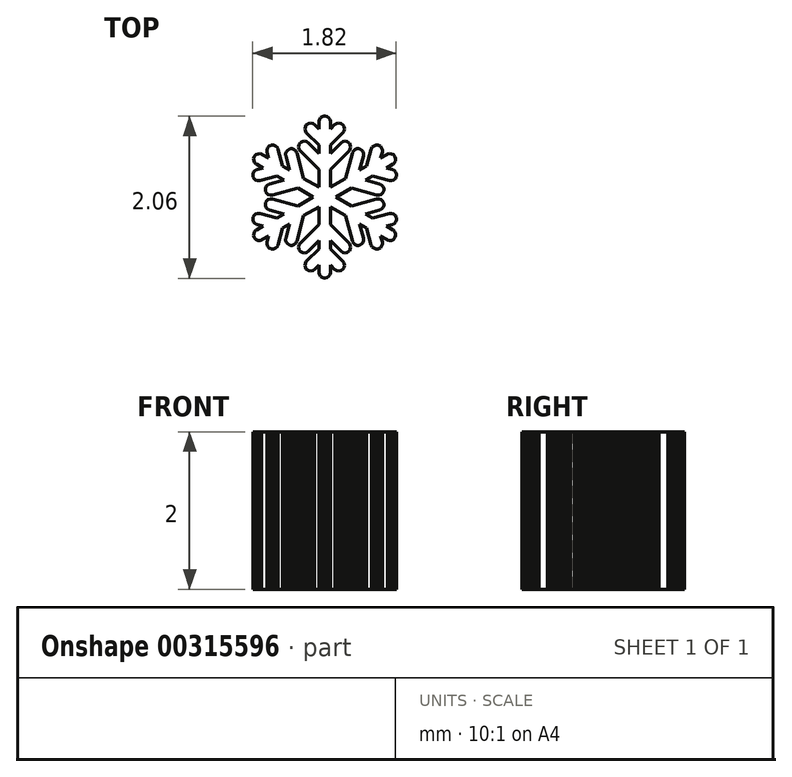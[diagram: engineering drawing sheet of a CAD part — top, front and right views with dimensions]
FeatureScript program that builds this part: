
annotation { "Feature Type Name" : "Feature", "Feature Type Description" : "" }
export const myFeature = defineFeature(function(context is Context, id is Id, definition is map)
    precondition{}
    {
        {
            var Q0;
            Q0=qCreatedBy(makeId("Top.planeOp"),FACE);
            var sketch = newSketch(context, id + "F0", { "sketchPlane" : qUnion([Q0])});
            skLineSegment(sketch, "E0", {"start": v(-2.78, 1.2) * mm, "end": v(-2.78, 3.11) * mm});
            skLineSegment(sketch, "E1", {"start": v(-2.78, 3.11) * mm, "end": v(-2.78, 3.12) * mm});
            skLineSegment(sketch, "E2", {"start": v(-2.78, 3.12) * mm, "end": v(-2.79, 3.14) * mm});
            skLineSegment(sketch, "E3", {"start": v(-2.79, 3.14) * mm, "end": v(-2.8, 3.16) * mm});
            skLineSegment(sketch, "E4", {"start": v(-2.8, 3.16) * mm, "end": v(-2.83, 3.18) * mm});
            skLineSegment(sketch, "E5", {"start": v(-2.83, 3.18) * mm, "end": v(-2.85, 3.18) * mm});
            skLineSegment(sketch, "E6", {"start": v(-2.85, 3.18) * mm, "end": v(-2.86, 3.18) * mm});
            skLineSegment(sketch, "E7", {"start": v(-2.86, 3.18) * mm, "end": v(-2.86, 3.18) * mm});
            skLineSegment(sketch, "E8", {"start": v(-2.86, 3.18) * mm, "end": v(-2.89, 3.18) * mm});
            skLineSegment(sketch, "E9", {"start": v(-2.89, 3.18) * mm, "end": v(-2.9, 3.16) * mm});
            skLineSegment(sketch, "E10", {"start": v(-2.9, 3.16) * mm, "end": v(-2.92, 3.14) * mm});
            skLineSegment(sketch, "E11", {"start": v(-2.92, 3.14) * mm, "end": v(-2.93, 3.12) * mm});
            skLineSegment(sketch, "E12", {"start": v(-2.93, 3.12) * mm, "end": v(-2.93, 3.11) * mm});
            skLineSegment(sketch, "E13", {"start": v(-2.93, 3.11) * mm, "end": v(-2.93, 1.2) * mm});
            skLineSegment(sketch, "E14", {"start": v(-2.93, 1.2) * mm, "end": v(-2.93, 1.19) * mm});
            skLineSegment(sketch, "E15", {"start": v(-2.93, 1.19) * mm, "end": v(-2.92, 1.17) * mm});
            skLineSegment(sketch, "E16", {"start": v(-2.92, 1.17) * mm, "end": v(-2.9, 1.14) * mm});
            skLineSegment(sketch, "E17", {"start": v(-2.9, 1.14) * mm, "end": v(-2.89, 1.13) * mm});
            skLineSegment(sketch, "E18", {"start": v(-2.89, 1.13) * mm, "end": v(-2.86, 1.12) * mm});
            skLineSegment(sketch, "E19", {"start": v(-2.86, 1.12) * mm, "end": v(-2.86, 1.12) * mm});
            skLineSegment(sketch, "E20", {"start": v(-2.86, 1.12) * mm, "end": v(-2.85, 1.12) * mm});
            skLineSegment(sketch, "E21", {"start": v(-2.85, 1.12) * mm, "end": v(-2.83, 1.13) * mm});
            skLineSegment(sketch, "E22", {"start": v(-2.83, 1.13) * mm, "end": v(-2.8, 1.14) * mm});
            skLineSegment(sketch, "E23", {"start": v(-2.8, 1.14) * mm, "end": v(-2.79, 1.17) * mm});
            skLineSegment(sketch, "E24", {"start": v(-2.79, 1.17) * mm, "end": v(-2.78, 1.19) * mm});
            skLineSegment(sketch, "E25", {"start": v(-2.78, 1.19) * mm, "end": v(-2.78, 1.2) * mm});
            skLineSegment(sketch, "E26", {"start": v(-2.55, 2.84) * mm, "end": v(-2.55, 2.85) * mm});
            skLineSegment(sketch, "E27", {"start": v(-2.55, 2.85) * mm, "end": v(-2.57, 2.86) * mm});
            skLineSegment(sketch, "E28", {"start": v(-2.57, 2.86) * mm, "end": v(-2.6, 2.86) * mm});
            skLineSegment(sketch, "E29", {"start": v(-2.6, 2.86) * mm, "end": v(-2.63, 2.86) * mm});
            skLineSegment(sketch, "E30", {"start": v(-2.63, 2.86) * mm, "end": v(-2.65, 2.85) * mm});
            skLineSegment(sketch, "E31", {"start": v(-2.65, 2.85) * mm, "end": v(-2.65, 2.84) * mm});
            skLineSegment(sketch, "E32", {"start": v(-2.65, 2.84) * mm, "end": v(-2.86, 2.64) * mm});
            skLineSegment(sketch, "E33", {"start": v(-2.86, 2.64) * mm, "end": v(-3.06, 2.84) * mm});
            skLineSegment(sketch, "E34", {"start": v(-3.06, 2.84) * mm, "end": v(-3.07, 2.85) * mm});
            skLineSegment(sketch, "E35", {"start": v(-3.07, 2.85) * mm, "end": v(-3.09, 2.86) * mm});
            skLineSegment(sketch, "E36", {"start": v(-3.09, 2.86) * mm, "end": v(-3.11, 2.86) * mm});
            skLineSegment(sketch, "E37", {"start": v(-3.11, 2.86) * mm, "end": v(-3.14, 2.86) * mm});
            skLineSegment(sketch, "E38", {"start": v(-3.14, 2.86) * mm, "end": v(-3.16, 2.85) * mm});
            skLineSegment(sketch, "E39", {"start": v(-3.16, 2.85) * mm, "end": v(-3.17, 2.84) * mm});
            skLineSegment(sketch, "E40", {"start": v(-3.17, 2.84) * mm, "end": v(-3.17, 2.84) * mm});
            skLineSegment(sketch, "E41", {"start": v(-3.17, 2.84) * mm, "end": v(-3.18, 2.82) * mm});
            skLineSegment(sketch, "E42", {"start": v(-3.18, 2.82) * mm, "end": v(-3.19, 2.79) * mm});
            skLineSegment(sketch, "E43", {"start": v(-3.19, 2.79) * mm, "end": v(-3.18, 2.76) * mm});
            skLineSegment(sketch, "E44", {"start": v(-3.18, 2.76) * mm, "end": v(-3.17, 2.74) * mm});
            skLineSegment(sketch, "E45", {"start": v(-3.17, 2.74) * mm, "end": v(-3.17, 2.74) * mm});
            skLineSegment(sketch, "E46", {"start": v(-3.17, 2.74) * mm, "end": v(-2.91, 2.48) * mm});
            skLineSegment(sketch, "E47", {"start": v(-2.91, 2.48) * mm, "end": v(-2.9, 2.48) * mm});
            skLineSegment(sketch, "E48", {"start": v(-2.9, 2.48) * mm, "end": v(-2.89, 2.47) * mm});
            skLineSegment(sketch, "E49", {"start": v(-2.89, 2.47) * mm, "end": v(-2.86, 2.46) * mm});
            skLineSegment(sketch, "E50", {"start": v(-2.86, 2.46) * mm, "end": v(-2.86, 2.46) * mm});
            skLineSegment(sketch, "E51", {"start": v(-2.86, 2.46) * mm, "end": v(-2.85, 2.46) * mm});
            skLineSegment(sketch, "E52", {"start": v(-2.85, 2.46) * mm, "end": v(-2.83, 2.47) * mm});
            skLineSegment(sketch, "E53", {"start": v(-2.83, 2.47) * mm, "end": v(-2.8, 2.48) * mm});
            skLineSegment(sketch, "E54", {"start": v(-2.8, 2.48) * mm, "end": v(-2.8, 2.48) * mm});
            skLineSegment(sketch, "E55", {"start": v(-2.8, 2.48) * mm, "end": v(-2.55, 2.74) * mm});
            skLineSegment(sketch, "E56", {"start": v(-2.55, 2.74) * mm, "end": v(-2.54, 2.74) * mm});
            skLineSegment(sketch, "E57", {"start": v(-2.54, 2.74) * mm, "end": v(-2.53, 2.76) * mm});
            skLineSegment(sketch, "E58", {"start": v(-2.53, 2.76) * mm, "end": v(-2.53, 2.79) * mm});
            skLineSegment(sketch, "E59", {"start": v(-2.53, 2.79) * mm, "end": v(-2.53, 2.82) * mm});
            skLineSegment(sketch, "E60", {"start": v(-2.53, 2.82) * mm, "end": v(-2.54, 2.84) * mm});
            skLineSegment(sketch, "E61", {"start": v(-2.54, 2.84) * mm, "end": v(-2.55, 2.84) * mm});
            skLineSegment(sketch, "E62", {"start": v(-2.63, 3.07) * mm, "end": v(-2.63, 3.08) * mm});
            skLineSegment(sketch, "E63", {"start": v(-2.63, 3.08) * mm, "end": v(-2.65, 3.09) * mm});
            skLineSegment(sketch, "E64", {"start": v(-2.65, 3.09) * mm, "end": v(-2.68, 3.1) * mm});
            skLineSegment(sketch, "E65", {"start": v(-2.68, 3.1) * mm, "end": v(-2.7, 3.09) * mm});
            skLineSegment(sketch, "E66", {"start": v(-2.7, 3.09) * mm, "end": v(-2.73, 3.08) * mm});
            skLineSegment(sketch, "E67", {"start": v(-2.73, 3.08) * mm, "end": v(-2.73, 3.07) * mm});
            skLineSegment(sketch, "E68", {"start": v(-2.73, 3.07) * mm, "end": v(-2.86, 2.94) * mm});
            skLineSegment(sketch, "E69", {"start": v(-2.86, 2.94) * mm, "end": v(-2.98, 3.07) * mm});
            skLineSegment(sketch, "E70", {"start": v(-2.98, 3.07) * mm, "end": v(-2.99, 3.08) * mm});
            skLineSegment(sketch, "E71", {"start": v(-2.99, 3.08) * mm, "end": v(-3, 3.09) * mm});
            skLineSegment(sketch, "E72", {"start": v(-3, 3.09) * mm, "end": v(-3.04, 3.1) * mm});
            skLineSegment(sketch, "E73", {"start": v(-3.04, 3.1) * mm, "end": v(-3.06, 3.09) * mm});
            skLineSegment(sketch, "E74", {"start": v(-3.06, 3.09) * mm, "end": v(-3.08, 3.08) * mm});
            skLineSegment(sketch, "E75", {"start": v(-3.08, 3.08) * mm, "end": v(-3.09, 3.07) * mm});
            skLineSegment(sketch, "E76", {"start": v(-3.09, 3.07) * mm, "end": v(-3.1, 3.07) * mm});
            skLineSegment(sketch, "E77", {"start": v(-3.1, 3.07) * mm, "end": v(-3.1, 3.05) * mm});
            skLineSegment(sketch, "E78", {"start": v(-3.1, 3.05) * mm, "end": v(-3.1, 3.02) * mm});
            skLineSegment(sketch, "E79", {"start": v(-3.1, 3.02) * mm, "end": v(-3.1, 3) * mm});
            skLineSegment(sketch, "E80", {"start": v(-3.1, 3) * mm, "end": v(-3.1, 2.97) * mm});
            skLineSegment(sketch, "E81", {"start": v(-3.1, 2.97) * mm, "end": v(-3.09, 2.97) * mm});
            skLineSegment(sketch, "E82", {"start": v(-3.09, 2.97) * mm, "end": v(-2.91, 2.8) * mm});
            skLineSegment(sketch, "E83", {"start": v(-2.91, 2.8) * mm, "end": v(-2.9, 2.79) * mm});
            skLineSegment(sketch, "E84", {"start": v(-2.9, 2.79) * mm, "end": v(-2.89, 2.78) * mm});
            skLineSegment(sketch, "E85", {"start": v(-2.89, 2.78) * mm, "end": v(-2.86, 2.77) * mm});
            skLineSegment(sketch, "E86", {"start": v(-2.86, 2.77) * mm, "end": v(-2.86, 2.77) * mm});
            skLineSegment(sketch, "E87", {"start": v(-2.86, 2.77) * mm, "end": v(-2.85, 2.77) * mm});
            skLineSegment(sketch, "E88", {"start": v(-2.85, 2.77) * mm, "end": v(-2.83, 2.78) * mm});
            skLineSegment(sketch, "E89", {"start": v(-2.83, 2.78) * mm, "end": v(-2.8, 2.79) * mm});
            skLineSegment(sketch, "E90", {"start": v(-2.8, 2.79) * mm, "end": v(-2.8, 2.8) * mm});
            skLineSegment(sketch, "E91", {"start": v(-2.8, 2.8) * mm, "end": v(-2.63, 2.97) * mm});
            skLineSegment(sketch, "E92", {"start": v(-2.63, 2.97) * mm, "end": v(-2.62, 2.97) * mm});
            skLineSegment(sketch, "E93", {"start": v(-2.62, 2.97) * mm, "end": v(-2.61, 3) * mm});
            skLineSegment(sketch, "E94", {"start": v(-2.61, 3) * mm, "end": v(-2.6, 3.02) * mm});
            skLineSegment(sketch, "E95", {"start": v(-2.6, 3.02) * mm, "end": v(-2.61, 3.05) * mm});
            skLineSegment(sketch, "E96", {"start": v(-2.61, 3.05) * mm, "end": v(-2.62, 3.07) * mm});
            skLineSegment(sketch, "E97", {"start": v(-2.62, 3.07) * mm, "end": v(-2.63, 3.07) * mm});
            skLineSegment(sketch, "E98", {"start": v(-2.55, 1.46) * mm, "end": v(-2.55, 1.46) * mm});
            skLineSegment(sketch, "E99", {"start": v(-2.55, 1.46) * mm, "end": v(-2.57, 1.45) * mm});
            skLineSegment(sketch, "E100", {"start": v(-2.57, 1.45) * mm, "end": v(-2.6, 1.44) * mm});
            skLineSegment(sketch, "E101", {"start": v(-2.6, 1.44) * mm, "end": v(-2.63, 1.45) * mm});
            skLineSegment(sketch, "E102", {"start": v(-2.63, 1.45) * mm, "end": v(-2.65, 1.46) * mm});
            skLineSegment(sketch, "E103", {"start": v(-2.65, 1.46) * mm, "end": v(-2.65, 1.46) * mm});
            skLineSegment(sketch, "E104", {"start": v(-2.65, 1.46) * mm, "end": v(-2.86, 1.67) * mm});
            skLineSegment(sketch, "E105", {"start": v(-2.86, 1.67) * mm, "end": v(-3.06, 1.46) * mm});
            skLineSegment(sketch, "E106", {"start": v(-3.06, 1.46) * mm, "end": v(-3.07, 1.46) * mm});
            skLineSegment(sketch, "E107", {"start": v(-3.07, 1.46) * mm, "end": v(-3.09, 1.45) * mm});
            skLineSegment(sketch, "E108", {"start": v(-3.09, 1.45) * mm, "end": v(-3.11, 1.44) * mm});
            skLineSegment(sketch, "E109", {"start": v(-3.11, 1.44) * mm, "end": v(-3.14, 1.45) * mm});
            skLineSegment(sketch, "E110", {"start": v(-3.14, 1.45) * mm, "end": v(-3.16, 1.46) * mm});
            skLineSegment(sketch, "E111", {"start": v(-3.16, 1.46) * mm, "end": v(-3.17, 1.46) * mm});
            skLineSegment(sketch, "E112", {"start": v(-3.17, 1.46) * mm, "end": v(-3.17, 1.47) * mm});
            skLineSegment(sketch, "E113", {"start": v(-3.17, 1.47) * mm, "end": v(-3.18, 1.49) * mm});
            skLineSegment(sketch, "E114", {"start": v(-3.18, 1.49) * mm, "end": v(-3.19, 1.52) * mm});
            skLineSegment(sketch, "E115", {"start": v(-3.19, 1.52) * mm, "end": v(-3.18, 1.54) * mm});
            skLineSegment(sketch, "E116", {"start": v(-3.18, 1.54) * mm, "end": v(-3.17, 1.56) * mm});
            skLineSegment(sketch, "E117", {"start": v(-3.17, 1.56) * mm, "end": v(-3.17, 1.57) * mm});
            skLineSegment(sketch, "E118", {"start": v(-3.17, 1.57) * mm, "end": v(-2.91, 1.82) * mm});
            skLineSegment(sketch, "E119", {"start": v(-2.91, 1.82) * mm, "end": v(-2.9, 1.83) * mm});
            skLineSegment(sketch, "E120", {"start": v(-2.9, 1.83) * mm, "end": v(-2.89, 1.84) * mm});
            skLineSegment(sketch, "E121", {"start": v(-2.89, 1.84) * mm, "end": v(-2.86, 1.84) * mm});
            skLineSegment(sketch, "E122", {"start": v(-2.86, 1.84) * mm, "end": v(-2.86, 1.84) * mm});
            skLineSegment(sketch, "E123", {"start": v(-2.86, 1.84) * mm, "end": v(-2.85, 1.84) * mm});
            skLineSegment(sketch, "E124", {"start": v(-2.85, 1.84) * mm, "end": v(-2.83, 1.84) * mm});
            skLineSegment(sketch, "E125", {"start": v(-2.83, 1.84) * mm, "end": v(-2.8, 1.83) * mm});
            skLineSegment(sketch, "E126", {"start": v(-2.8, 1.83) * mm, "end": v(-2.8, 1.82) * mm});
            skLineSegment(sketch, "E127", {"start": v(-2.8, 1.82) * mm, "end": v(-2.55, 1.57) * mm});
            skLineSegment(sketch, "E128", {"start": v(-2.55, 1.57) * mm, "end": v(-2.54, 1.56) * mm});
            skLineSegment(sketch, "E129", {"start": v(-2.54, 1.56) * mm, "end": v(-2.53, 1.54) * mm});
            skLineSegment(sketch, "E130", {"start": v(-2.53, 1.54) * mm, "end": v(-2.53, 1.52) * mm});
            skLineSegment(sketch, "E131", {"start": v(-2.53, 1.52) * mm, "end": v(-2.53, 1.49) * mm});
            skLineSegment(sketch, "E132", {"start": v(-2.53, 1.49) * mm, "end": v(-2.54, 1.47) * mm});
            skLineSegment(sketch, "E133", {"start": v(-2.54, 1.47) * mm, "end": v(-2.55, 1.46) * mm});
            skLineSegment(sketch, "E134", {"start": v(-2.63, 1.23) * mm, "end": v(-2.63, 1.23) * mm});
            skLineSegment(sketch, "E135", {"start": v(-2.63, 1.23) * mm, "end": v(-2.65, 1.22) * mm});
            skLineSegment(sketch, "E136", {"start": v(-2.65, 1.22) * mm, "end": v(-2.68, 1.21) * mm});
            skLineSegment(sketch, "E137", {"start": v(-2.68, 1.21) * mm, "end": v(-2.7, 1.22) * mm});
            skLineSegment(sketch, "E138", {"start": v(-2.7, 1.22) * mm, "end": v(-2.73, 1.23) * mm});
            skLineSegment(sketch, "E139", {"start": v(-2.73, 1.23) * mm, "end": v(-2.73, 1.23) * mm});
            skLineSegment(sketch, "E140", {"start": v(-2.73, 1.23) * mm, "end": v(-2.86, 1.36) * mm});
            skLineSegment(sketch, "E141", {"start": v(-2.86, 1.36) * mm, "end": v(-2.98, 1.23) * mm});
            skLineSegment(sketch, "E142", {"start": v(-2.98, 1.23) * mm, "end": v(-2.99, 1.23) * mm});
            skLineSegment(sketch, "E143", {"start": v(-2.99, 1.23) * mm, "end": v(-3, 1.22) * mm});
            skLineSegment(sketch, "E144", {"start": v(-3, 1.22) * mm, "end": v(-3.04, 1.21) * mm});
            skLineSegment(sketch, "E145", {"start": v(-3.04, 1.21) * mm, "end": v(-3.06, 1.22) * mm});
            skLineSegment(sketch, "E146", {"start": v(-3.06, 1.22) * mm, "end": v(-3.08, 1.23) * mm});
            skLineSegment(sketch, "E147", {"start": v(-3.08, 1.23) * mm, "end": v(-3.09, 1.23) * mm});
            skLineSegment(sketch, "E148", {"start": v(-3.09, 1.23) * mm, "end": v(-3.1, 1.24) * mm});
            skLineSegment(sketch, "E149", {"start": v(-3.1, 1.24) * mm, "end": v(-3.1, 1.26) * mm});
            skLineSegment(sketch, "E150", {"start": v(-3.1, 1.26) * mm, "end": v(-3.1, 1.29) * mm});
            skLineSegment(sketch, "E151", {"start": v(-3.1, 1.29) * mm, "end": v(-3.1, 1.31) * mm});
            skLineSegment(sketch, "E152", {"start": v(-3.1, 1.31) * mm, "end": v(-3.1, 1.33) * mm});
            skLineSegment(sketch, "E153", {"start": v(-3.1, 1.33) * mm, "end": v(-3.09, 1.34) * mm});
            skLineSegment(sketch, "E154", {"start": v(-3.09, 1.34) * mm, "end": v(-2.91, 1.51) * mm});
            skLineSegment(sketch, "E155", {"start": v(-2.91, 1.51) * mm, "end": v(-2.9, 1.52) * mm});
            skLineSegment(sketch, "E156", {"start": v(-2.9, 1.52) * mm, "end": v(-2.89, 1.53) * mm});
            skLineSegment(sketch, "E157", {"start": v(-2.89, 1.53) * mm, "end": v(-2.86, 1.53) * mm});
            skLineSegment(sketch, "E158", {"start": v(-2.86, 1.53) * mm, "end": v(-2.86, 1.53) * mm});
            skLineSegment(sketch, "E159", {"start": v(-2.86, 1.53) * mm, "end": v(-2.85, 1.53) * mm});
            skLineSegment(sketch, "E160", {"start": v(-2.85, 1.53) * mm, "end": v(-2.83, 1.53) * mm});
            skLineSegment(sketch, "E161", {"start": v(-2.83, 1.53) * mm, "end": v(-2.8, 1.52) * mm});
            skLineSegment(sketch, "E162", {"start": v(-2.8, 1.52) * mm, "end": v(-2.8, 1.51) * mm});
            skLineSegment(sketch, "E163", {"start": v(-2.8, 1.51) * mm, "end": v(-2.63, 1.34) * mm});
            skLineSegment(sketch, "E164", {"start": v(-2.63, 1.34) * mm, "end": v(-2.62, 1.33) * mm});
            skLineSegment(sketch, "E165", {"start": v(-2.62, 1.33) * mm, "end": v(-2.61, 1.31) * mm});
            skLineSegment(sketch, "E166", {"start": v(-2.61, 1.31) * mm, "end": v(-2.6, 1.29) * mm});
            skLineSegment(sketch, "E167", {"start": v(-2.6, 1.29) * mm, "end": v(-2.61, 1.26) * mm});
            skLineSegment(sketch, "E168", {"start": v(-2.61, 1.26) * mm, "end": v(-2.62, 1.24) * mm});
            skLineSegment(sketch, "E169", {"start": v(-2.62, 1.24) * mm, "end": v(-2.63, 1.23) * mm});
            skLineSegment(sketch, "E170", {"start": v(-2, 1.74) * mm, "end": v(-3.65, 2.7) * mm});
            skLineSegment(sketch, "E171", {"start": v(-3.65, 2.7) * mm, "end": v(-3.66, 2.7) * mm});
            skLineSegment(sketch, "E172", {"start": v(-3.66, 2.7) * mm, "end": v(-3.68, 2.7) * mm});
            skLineSegment(sketch, "E173", {"start": v(-3.68, 2.7) * mm, "end": v(-3.7, 2.7) * mm});
            skLineSegment(sketch, "E174", {"start": v(-3.7, 2.7) * mm, "end": v(-3.73, 2.7) * mm});
            skLineSegment(sketch, "E175", {"start": v(-3.73, 2.7) * mm, "end": v(-3.75, 2.67) * mm});
            skLineSegment(sketch, "E176", {"start": v(-3.75, 2.67) * mm, "end": v(-3.75, 2.67) * mm});
            skLineSegment(sketch, "E177", {"start": v(-3.75, 2.67) * mm, "end": v(-3.75, 2.66) * mm});
            skLineSegment(sketch, "E178", {"start": v(-3.75, 2.66) * mm, "end": v(-3.76, 2.64) * mm});
            skLineSegment(sketch, "E179", {"start": v(-3.76, 2.64) * mm, "end": v(-3.76, 2.61) * mm});
            skLineSegment(sketch, "E180", {"start": v(-3.76, 2.61) * mm, "end": v(-3.74, 2.59) * mm});
            skLineSegment(sketch, "E181", {"start": v(-3.74, 2.59) * mm, "end": v(-3.73, 2.57) * mm});
            skLineSegment(sketch, "E182", {"start": v(-3.73, 2.57) * mm, "end": v(-3.72, 2.57) * mm});
            skLineSegment(sketch, "E183", {"start": v(-3.72, 2.57) * mm, "end": v(-2.06, 1.61) * mm});
            skLineSegment(sketch, "E184", {"start": v(-2.06, 1.61) * mm, "end": v(-2.06, 1.6) * mm});
            skLineSegment(sketch, "E185", {"start": v(-2.06, 1.6) * mm, "end": v(-2.04, 1.6) * mm});
            skLineSegment(sketch, "E186", {"start": v(-2.04, 1.6) * mm, "end": v(-2, 1.6) * mm});
            skLineSegment(sketch, "E187", {"start": v(-2, 1.6) * mm, "end": v(-1.98, 1.62) * mm});
            skLineSegment(sketch, "E188", {"start": v(-1.98, 1.62) * mm, "end": v(-1.97, 1.63) * mm});
            skLineSegment(sketch, "E189", {"start": v(-1.97, 1.63) * mm, "end": v(-1.96, 1.64) * mm});
            skLineSegment(sketch, "E190", {"start": v(-1.96, 1.64) * mm, "end": v(-1.96, 1.64) * mm});
            skLineSegment(sketch, "E191", {"start": v(-1.96, 1.64) * mm, "end": v(-1.95, 1.66) * mm});
            skLineSegment(sketch, "E192", {"start": v(-1.95, 1.66) * mm, "end": v(-1.96, 1.7) * mm});
            skLineSegment(sketch, "E193", {"start": v(-1.96, 1.7) * mm, "end": v(-1.97, 1.72) * mm});
            skLineSegment(sketch, "E194", {"start": v(-1.97, 1.72) * mm, "end": v(-1.98, 1.73) * mm});
            skLineSegment(sketch, "E195", {"start": v(-1.98, 1.73) * mm, "end": v(-2, 1.74) * mm});
            skLineSegment(sketch, "E196", {"start": v(-3.3, 2.76) * mm, "end": v(-3.3, 2.76) * mm});
            skLineSegment(sketch, "E197", {"start": v(-3.3, 2.76) * mm, "end": v(-3.32, 2.75) * mm});
            skLineSegment(sketch, "E198", {"start": v(-3.32, 2.75) * mm, "end": v(-3.34, 2.73) * mm});
            skLineSegment(sketch, "E199", {"start": v(-3.34, 2.73) * mm, "end": v(-3.35, 2.7) * mm});
            skLineSegment(sketch, "E200", {"start": v(-3.35, 2.7) * mm, "end": v(-3.35, 2.68) * mm});
            skLineSegment(sketch, "E201", {"start": v(-3.35, 2.68) * mm, "end": v(-3.35, 2.68) * mm});
            skLineSegment(sketch, "E202", {"start": v(-3.35, 2.68) * mm, "end": v(-3.27, 2.4) * mm});
            skLineSegment(sketch, "E203", {"start": v(-3.27, 2.4) * mm, "end": v(-3.56, 2.32) * mm});
            skLineSegment(sketch, "E204", {"start": v(-3.56, 2.32) * mm, "end": v(-3.56, 2.32) * mm});
            skLineSegment(sketch, "E205", {"start": v(-3.56, 2.32) * mm, "end": v(-3.58, 2.3) * mm});
            skLineSegment(sketch, "E206", {"start": v(-3.58, 2.3) * mm, "end": v(-3.6, 2.29) * mm});
            skLineSegment(sketch, "E207", {"start": v(-3.6, 2.29) * mm, "end": v(-3.6, 2.26) * mm});
            skLineSegment(sketch, "E208", {"start": v(-3.6, 2.26) * mm, "end": v(-3.6, 2.24) * mm});
            skLineSegment(sketch, "E209", {"start": v(-3.6, 2.24) * mm, "end": v(-3.6, 2.23) * mm});
            skLineSegment(sketch, "E210", {"start": v(-3.6, 2.23) * mm, "end": v(-3.6, 2.22) * mm});
            skLineSegment(sketch, "E211", {"start": v(-3.6, 2.22) * mm, "end": v(-3.6, 2.2) * mm});
            skLineSegment(sketch, "E212", {"start": v(-3.6, 2.2) * mm, "end": v(-3.57, 2.19) * mm});
            skLineSegment(sketch, "E213", {"start": v(-3.57, 2.19) * mm, "end": v(-3.55, 2.18) * mm});
            skLineSegment(sketch, "E214", {"start": v(-3.55, 2.18) * mm, "end": v(-3.53, 2.18) * mm});
            skLineSegment(sketch, "E215", {"start": v(-3.53, 2.18) * mm, "end": v(-3.52, 2.18) * mm});
            skLineSegment(sketch, "E216", {"start": v(-3.52, 2.18) * mm, "end": v(-3.17, 2.27) * mm});
            skLineSegment(sketch, "E217", {"start": v(-3.17, 2.27) * mm, "end": v(-3.17, 2.27) * mm});
            skLineSegment(sketch, "E218", {"start": v(-3.17, 2.27) * mm, "end": v(-3.14, 2.29) * mm});
            skLineSegment(sketch, "E219", {"start": v(-3.14, 2.29) * mm, "end": v(-3.13, 2.3) * mm});
            skLineSegment(sketch, "E220", {"start": v(-3.13, 2.3) * mm, "end": v(-3.13, 2.3) * mm});
            skLineSegment(sketch, "E221", {"start": v(-3.13, 2.3) * mm, "end": v(-3.12, 2.31) * mm});
            skLineSegment(sketch, "E222", {"start": v(-3.12, 2.31) * mm, "end": v(-3.11, 2.34) * mm});
            skLineSegment(sketch, "E223", {"start": v(-3.11, 2.34) * mm, "end": v(-3.12, 2.36) * mm});
            skLineSegment(sketch, "E224", {"start": v(-3.12, 2.36) * mm, "end": v(-3.12, 2.37) * mm});
            skLineSegment(sketch, "E225", {"start": v(-3.12, 2.37) * mm, "end": v(-3.2, 2.71) * mm});
            skLineSegment(sketch, "E226", {"start": v(-3.2, 2.71) * mm, "end": v(-3.21, 2.72) * mm});
            skLineSegment(sketch, "E227", {"start": v(-3.21, 2.72) * mm, "end": v(-3.22, 2.74) * mm});
            skLineSegment(sketch, "E228", {"start": v(-3.22, 2.74) * mm, "end": v(-3.24, 2.76) * mm});
            skLineSegment(sketch, "E229", {"start": v(-3.24, 2.76) * mm, "end": v(-3.27, 2.77) * mm});
            skLineSegment(sketch, "E230", {"start": v(-3.27, 2.77) * mm, "end": v(-3.3, 2.77) * mm});
            skLineSegment(sketch, "E231", {"start": v(-3.3, 2.77) * mm, "end": v(-3.3, 2.76) * mm});
            skLineSegment(sketch, "E232", {"start": v(-3.54, 2.81) * mm, "end": v(-3.54, 2.8) * mm});
            skLineSegment(sketch, "E233", {"start": v(-3.54, 2.8) * mm, "end": v(-3.56, 2.8) * mm});
            skLineSegment(sketch, "E234", {"start": v(-3.56, 2.8) * mm, "end": v(-3.58, 2.78) * mm});
            skLineSegment(sketch, "E235", {"start": v(-3.58, 2.78) * mm, "end": v(-3.6, 2.75) * mm});
            skLineSegment(sketch, "E236", {"start": v(-3.6, 2.75) * mm, "end": v(-3.6, 2.73) * mm});
            skLineSegment(sketch, "E237", {"start": v(-3.6, 2.73) * mm, "end": v(-3.59, 2.72) * mm});
            skLineSegment(sketch, "E238", {"start": v(-3.59, 2.72) * mm, "end": v(-3.54, 2.55) * mm});
            skLineSegment(sketch, "E239", {"start": v(-3.54, 2.55) * mm, "end": v(-3.72, 2.5) * mm});
            skLineSegment(sketch, "E240", {"start": v(-3.72, 2.5) * mm, "end": v(-3.72, 2.5) * mm});
            skLineSegment(sketch, "E241", {"start": v(-3.72, 2.5) * mm, "end": v(-3.74, 2.49) * mm});
            skLineSegment(sketch, "E242", {"start": v(-3.74, 2.49) * mm, "end": v(-3.76, 2.47) * mm});
            skLineSegment(sketch, "E243", {"start": v(-3.76, 2.47) * mm, "end": v(-3.77, 2.44) * mm});
            skLineSegment(sketch, "E244", {"start": v(-3.77, 2.44) * mm, "end": v(-3.77, 2.42) * mm});
            skLineSegment(sketch, "E245", {"start": v(-3.77, 2.42) * mm, "end": v(-3.77, 2.41) * mm});
            skLineSegment(sketch, "E246", {"start": v(-3.77, 2.41) * mm, "end": v(-3.77, 2.4) * mm});
            skLineSegment(sketch, "E247", {"start": v(-3.77, 2.4) * mm, "end": v(-3.75, 2.39) * mm});
            skLineSegment(sketch, "E248", {"start": v(-3.75, 2.39) * mm, "end": v(-3.73, 2.37) * mm});
            skLineSegment(sketch, "E249", {"start": v(-3.73, 2.37) * mm, "end": v(-3.7, 2.36) * mm});
            skLineSegment(sketch, "E250", {"start": v(-3.7, 2.36) * mm, "end": v(-3.68, 2.36) * mm});
            skLineSegment(sketch, "E251", {"start": v(-3.68, 2.36) * mm, "end": v(-3.68, 2.36) * mm});
            skLineSegment(sketch, "E252", {"start": v(-3.68, 2.36) * mm, "end": v(-3.44, 2.43) * mm});
            skLineSegment(sketch, "E253", {"start": v(-3.44, 2.43) * mm, "end": v(-3.43, 2.43) * mm});
            skLineSegment(sketch, "E254", {"start": v(-3.43, 2.43) * mm, "end": v(-3.41, 2.44) * mm});
            skLineSegment(sketch, "E255", {"start": v(-3.41, 2.44) * mm, "end": v(-3.4, 2.46) * mm});
            skLineSegment(sketch, "E256", {"start": v(-3.4, 2.46) * mm, "end": v(-3.4, 2.46) * mm});
            skLineSegment(sketch, "E257", {"start": v(-3.4, 2.46) * mm, "end": v(-3.4, 2.47) * mm});
            skLineSegment(sketch, "E258", {"start": v(-3.4, 2.47) * mm, "end": v(-3.38, 2.49) * mm});
            skLineSegment(sketch, "E259", {"start": v(-3.38, 2.49) * mm, "end": v(-3.38, 2.52) * mm});
            skLineSegment(sketch, "E260", {"start": v(-3.38, 2.52) * mm, "end": v(-3.38, 2.52) * mm});
            skLineSegment(sketch, "E261", {"start": v(-3.38, 2.52) * mm, "end": v(-3.45, 2.76) * mm});
            skLineSegment(sketch, "E262", {"start": v(-3.45, 2.76) * mm, "end": v(-3.45, 2.77) * mm});
            skLineSegment(sketch, "E263", {"start": v(-3.45, 2.77) * mm, "end": v(-3.46, 2.79) * mm});
            skLineSegment(sketch, "E264", {"start": v(-3.46, 2.79) * mm, "end": v(-3.48, 2.8) * mm});
            skLineSegment(sketch, "E265", {"start": v(-3.48, 2.8) * mm, "end": v(-3.5, 2.81) * mm});
            skLineSegment(sketch, "E266", {"start": v(-3.5, 2.81) * mm, "end": v(-3.53, 2.81) * mm});
            skLineSegment(sketch, "E267", {"start": v(-3.53, 2.81) * mm, "end": v(-3.54, 2.81) * mm});
            skLineSegment(sketch, "E268", {"start": v(-2.1, 2.08) * mm, "end": v(-2.1, 2.07) * mm});
            skLineSegment(sketch, "E269", {"start": v(-2.1, 2.07) * mm, "end": v(-2.1, 2.05) * mm});
            skLineSegment(sketch, "E270", {"start": v(-2.1, 2.05) * mm, "end": v(-2.11, 2.02) * mm});
            skLineSegment(sketch, "E271", {"start": v(-2.11, 2.02) * mm, "end": v(-2.13, 2) * mm});
            skLineSegment(sketch, "E272", {"start": v(-2.13, 2) * mm, "end": v(-2.15, 1.99) * mm});
            skLineSegment(sketch, "E273", {"start": v(-2.15, 1.99) * mm, "end": v(-2.16, 1.99) * mm});
            skLineSegment(sketch, "E274", {"start": v(-2.16, 1.99) * mm, "end": v(-2.44, 1.91) * mm});
            skLineSegment(sketch, "E275", {"start": v(-2.44, 1.91) * mm, "end": v(-2.36, 1.63) * mm});
            skLineSegment(sketch, "E276", {"start": v(-2.36, 1.63) * mm, "end": v(-2.36, 1.62) * mm});
            skLineSegment(sketch, "E277", {"start": v(-2.36, 1.62) * mm, "end": v(-2.36, 1.6) * mm});
            skLineSegment(sketch, "E278", {"start": v(-2.36, 1.6) * mm, "end": v(-2.37, 1.58) * mm});
            skLineSegment(sketch, "E279", {"start": v(-2.37, 1.58) * mm, "end": v(-2.39, 1.55) * mm});
            skLineSegment(sketch, "E280", {"start": v(-2.39, 1.55) * mm, "end": v(-2.4, 1.54) * mm});
            skLineSegment(sketch, "E281", {"start": v(-2.4, 1.54) * mm, "end": v(-2.42, 1.54) * mm});
            skLineSegment(sketch, "E282", {"start": v(-2.42, 1.54) * mm, "end": v(-2.42, 1.54) * mm});
            skLineSegment(sketch, "E283", {"start": v(-2.42, 1.54) * mm, "end": v(-2.44, 1.54) * mm});
            skLineSegment(sketch, "E284", {"start": v(-2.44, 1.54) * mm, "end": v(-2.47, 1.55) * mm});
            skLineSegment(sketch, "E285", {"start": v(-2.47, 1.55) * mm, "end": v(-2.5, 1.57) * mm});
            skLineSegment(sketch, "E286", {"start": v(-2.5, 1.57) * mm, "end": v(-2.5, 1.59) * mm});
            skLineSegment(sketch, "E287", {"start": v(-2.5, 1.59) * mm, "end": v(-2.5, 1.6) * mm});
            skLineSegment(sketch, "E288", {"start": v(-2.5, 1.6) * mm, "end": v(-2.6, 1.94) * mm});
            skLineSegment(sketch, "E289", {"start": v(-2.6, 1.94) * mm, "end": v(-2.6, 1.95) * mm});
            skLineSegment(sketch, "E290", {"start": v(-2.6, 1.95) * mm, "end": v(-2.6, 1.97) * mm});
            skLineSegment(sketch, "E291", {"start": v(-2.6, 1.97) * mm, "end": v(-2.6, 2) * mm});
            skLineSegment(sketch, "E292", {"start": v(-2.6, 2) * mm, "end": v(-2.59, 2) * mm});
            skLineSegment(sketch, "E293", {"start": v(-2.59, 2) * mm, "end": v(-2.59, 2) * mm});
            skLineSegment(sketch, "E294", {"start": v(-2.59, 2) * mm, "end": v(-2.57, 2.02) * mm});
            skLineSegment(sketch, "E295", {"start": v(-2.57, 2.02) * mm, "end": v(-2.55, 2.03) * mm});
            skLineSegment(sketch, "E296", {"start": v(-2.55, 2.03) * mm, "end": v(-2.54, 2.03) * mm});
            skLineSegment(sketch, "E297", {"start": v(-2.54, 2.03) * mm, "end": v(-2.2, 2.13) * mm});
            skLineSegment(sketch, "E298", {"start": v(-2.2, 2.13) * mm, "end": v(-2.19, 2.13) * mm});
            skLineSegment(sketch, "E299", {"start": v(-2.19, 2.13) * mm, "end": v(-2.17, 2.13) * mm});
            skLineSegment(sketch, "E300", {"start": v(-2.17, 2.13) * mm, "end": v(-2.14, 2.12) * mm});
            skLineSegment(sketch, "E301", {"start": v(-2.14, 2.12) * mm, "end": v(-2.12, 2.1) * mm});
            skLineSegment(sketch, "E302", {"start": v(-2.12, 2.1) * mm, "end": v(-2.1, 2.08) * mm});
            skLineSegment(sketch, "E303", {"start": v(-2.1, 2.08) * mm, "end": v(-2.1, 2.08) * mm});
            skLineSegment(sketch, "E304", {"start": v(-1.95, 1.9) * mm, "end": v(-1.95, 1.89) * mm});
            skLineSegment(sketch, "E305", {"start": v(-1.95, 1.89) * mm, "end": v(-1.95, 1.86) * mm});
            skLineSegment(sketch, "E306", {"start": v(-1.95, 1.86) * mm, "end": v(-1.95, 1.84) * mm});
            skLineSegment(sketch, "E307", {"start": v(-1.95, 1.84) * mm, "end": v(-1.97, 1.82) * mm});
            skLineSegment(sketch, "E308", {"start": v(-1.97, 1.82) * mm, "end": v(-2, 1.8) * mm});
            skLineSegment(sketch, "E309", {"start": v(-2, 1.8) * mm, "end": v(-2, 1.8) * mm});
            skLineSegment(sketch, "E310", {"start": v(-2, 1.8) * mm, "end": v(-2.17, 1.76) * mm});
            skLineSegment(sketch, "E311", {"start": v(-2.17, 1.76) * mm, "end": v(-2.13, 1.58) * mm});
            skLineSegment(sketch, "E312", {"start": v(-2.13, 1.58) * mm, "end": v(-2.12, 1.58) * mm});
            skLineSegment(sketch, "E313", {"start": v(-2.12, 1.58) * mm, "end": v(-2.12, 1.56) * mm});
            skLineSegment(sketch, "E314", {"start": v(-2.12, 1.56) * mm, "end": v(-2.13, 1.53) * mm});
            skLineSegment(sketch, "E315", {"start": v(-2.13, 1.53) * mm, "end": v(-2.15, 1.5) * mm});
            skLineSegment(sketch, "E316", {"start": v(-2.15, 1.5) * mm, "end": v(-2.17, 1.5) * mm});
            skLineSegment(sketch, "E317", {"start": v(-2.17, 1.5) * mm, "end": v(-2.18, 1.5) * mm});
            skLineSegment(sketch, "E318", {"start": v(-2.18, 1.5) * mm, "end": v(-2.18, 1.5) * mm});
            skLineSegment(sketch, "E319", {"start": v(-2.18, 1.5) * mm, "end": v(-2.2, 1.5) * mm});
            skLineSegment(sketch, "E320", {"start": v(-2.2, 1.5) * mm, "end": v(-2.23, 1.5) * mm});
            skLineSegment(sketch, "E321", {"start": v(-2.23, 1.5) * mm, "end": v(-2.25, 1.52) * mm});
            skLineSegment(sketch, "E322", {"start": v(-2.25, 1.52) * mm, "end": v(-2.26, 1.54) * mm});
            skLineSegment(sketch, "E323", {"start": v(-2.26, 1.54) * mm, "end": v(-2.27, 1.55) * mm});
            skLineSegment(sketch, "E324", {"start": v(-2.27, 1.55) * mm, "end": v(-2.33, 1.79) * mm});
            skLineSegment(sketch, "E325", {"start": v(-2.33, 1.79) * mm, "end": v(-2.33, 1.8) * mm});
            skLineSegment(sketch, "E326", {"start": v(-2.33, 1.8) * mm, "end": v(-2.33, 1.82) * mm});
            skLineSegment(sketch, "E327", {"start": v(-2.33, 1.82) * mm, "end": v(-2.32, 1.84) * mm});
            skLineSegment(sketch, "E328", {"start": v(-2.32, 1.84) * mm, "end": v(-2.32, 1.84) * mm});
            skLineSegment(sketch, "E329", {"start": v(-2.32, 1.84) * mm, "end": v(-2.32, 1.85) * mm});
            skLineSegment(sketch, "E330", {"start": v(-2.32, 1.85) * mm, "end": v(-2.3, 1.87) * mm});
            skLineSegment(sketch, "E331", {"start": v(-2.3, 1.87) * mm, "end": v(-2.28, 1.88) * mm});
            skLineSegment(sketch, "E332", {"start": v(-2.28, 1.88) * mm, "end": v(-2.28, 1.88) * mm});
            skLineSegment(sketch, "E333", {"start": v(-2.28, 1.88) * mm, "end": v(-2.04, 1.94) * mm});
            skLineSegment(sketch, "E334", {"start": v(-2.04, 1.94) * mm, "end": v(-2.03, 1.95) * mm});
            skLineSegment(sketch, "E335", {"start": v(-2.03, 1.95) * mm, "end": v(-2, 1.95) * mm});
            skLineSegment(sketch, "E336", {"start": v(-2, 1.95) * mm, "end": v(-1.98, 1.94) * mm});
            skLineSegment(sketch, "E337", {"start": v(-1.98, 1.94) * mm, "end": v(-1.96, 1.92) * mm});
            skLineSegment(sketch, "E338", {"start": v(-1.96, 1.92) * mm, "end": v(-1.95, 1.9) * mm});
            skLineSegment(sketch, "E339", {"start": v(-1.95, 1.9) * mm, "end": v(-1.95, 1.9) * mm});
            skLineSegment(sketch, "E340", {"start": v(-2.06, 2.7) * mm, "end": v(-3.72, 1.74) * mm});
            skLineSegment(sketch, "E341", {"start": v(-3.72, 1.74) * mm, "end": v(-3.73, 1.73) * mm});
            skLineSegment(sketch, "E342", {"start": v(-3.73, 1.73) * mm, "end": v(-3.74, 1.72) * mm});
            skLineSegment(sketch, "E343", {"start": v(-3.74, 1.72) * mm, "end": v(-3.76, 1.7) * mm});
            skLineSegment(sketch, "E344", {"start": v(-3.76, 1.7) * mm, "end": v(-3.76, 1.66) * mm});
            skLineSegment(sketch, "E345", {"start": v(-3.76, 1.66) * mm, "end": v(-3.75, 1.64) * mm});
            skLineSegment(sketch, "E346", {"start": v(-3.75, 1.64) * mm, "end": v(-3.75, 1.64) * mm});
            skLineSegment(sketch, "E347", {"start": v(-3.75, 1.64) * mm, "end": v(-3.75, 1.63) * mm});
            skLineSegment(sketch, "E348", {"start": v(-3.75, 1.63) * mm, "end": v(-3.73, 1.62) * mm});
            skLineSegment(sketch, "E349", {"start": v(-3.73, 1.62) * mm, "end": v(-3.7, 1.6) * mm});
            skLineSegment(sketch, "E350", {"start": v(-3.7, 1.6) * mm, "end": v(-3.68, 1.6) * mm});
            skLineSegment(sketch, "E351", {"start": v(-3.68, 1.6) * mm, "end": v(-3.66, 1.6) * mm});
            skLineSegment(sketch, "E352", {"start": v(-3.66, 1.6) * mm, "end": v(-3.65, 1.61) * mm});
            skLineSegment(sketch, "E353", {"start": v(-3.65, 1.61) * mm, "end": v(-2, 2.57) * mm});
            skLineSegment(sketch, "E354", {"start": v(-2, 2.57) * mm, "end": v(-1.98, 2.57) * mm});
            skLineSegment(sketch, "E355", {"start": v(-1.98, 2.57) * mm, "end": v(-1.97, 2.59) * mm});
            skLineSegment(sketch, "E356", {"start": v(-1.97, 2.59) * mm, "end": v(-1.96, 2.61) * mm});
            skLineSegment(sketch, "E357", {"start": v(-1.96, 2.61) * mm, "end": v(-1.95, 2.64) * mm});
            skLineSegment(sketch, "E358", {"start": v(-1.95, 2.64) * mm, "end": v(-1.96, 2.66) * mm});
            skLineSegment(sketch, "E359", {"start": v(-1.96, 2.66) * mm, "end": v(-1.96, 2.67) * mm});
            skLineSegment(sketch, "E360", {"start": v(-1.96, 2.67) * mm, "end": v(-1.97, 2.67) * mm});
            skLineSegment(sketch, "E361", {"start": v(-1.97, 2.67) * mm, "end": v(-1.98, 2.7) * mm});
            skLineSegment(sketch, "E362", {"start": v(-1.98, 2.7) * mm, "end": v(-2, 2.7) * mm});
            skLineSegment(sketch, "E363", {"start": v(-2, 2.7) * mm, "end": v(-2.04, 2.7) * mm});
            skLineSegment(sketch, "E364", {"start": v(-2.04, 2.7) * mm, "end": v(-2.06, 2.7) * mm});
            skLineSegment(sketch, "E365", {"start": v(-2.06, 2.7) * mm, "end": v(-2.06, 2.7) * mm});
            skLineSegment(sketch, "E366", {"start": v(-3.6, 2.08) * mm, "end": v(-3.6, 2.07) * mm});
            skLineSegment(sketch, "E367", {"start": v(-3.6, 2.07) * mm, "end": v(-3.6, 2.05) * mm});
            skLineSegment(sketch, "E368", {"start": v(-3.6, 2.05) * mm, "end": v(-3.6, 2.02) * mm});
            skLineSegment(sketch, "E369", {"start": v(-3.6, 2.02) * mm, "end": v(-3.58, 2) * mm});
            skLineSegment(sketch, "E370", {"start": v(-3.58, 2) * mm, "end": v(-3.56, 1.99) * mm});
            skLineSegment(sketch, "E371", {"start": v(-3.56, 1.99) * mm, "end": v(-3.56, 1.99) * mm});
            skLineSegment(sketch, "E372", {"start": v(-3.56, 1.99) * mm, "end": v(-3.27, 1.91) * mm});
            skLineSegment(sketch, "E373", {"start": v(-3.27, 1.91) * mm, "end": v(-3.35, 1.63) * mm});
            skLineSegment(sketch, "E374", {"start": v(-3.35, 1.63) * mm, "end": v(-3.35, 1.62) * mm});
            skLineSegment(sketch, "E375", {"start": v(-3.35, 1.62) * mm, "end": v(-3.35, 1.6) * mm});
            skLineSegment(sketch, "E376", {"start": v(-3.35, 1.6) * mm, "end": v(-3.34, 1.58) * mm});
            skLineSegment(sketch, "E377", {"start": v(-3.34, 1.58) * mm, "end": v(-3.32, 1.55) * mm});
            skLineSegment(sketch, "E378", {"start": v(-3.32, 1.55) * mm, "end": v(-3.3, 1.54) * mm});
            skLineSegment(sketch, "E379", {"start": v(-3.3, 1.54) * mm, "end": v(-3.3, 1.54) * mm});
            skLineSegment(sketch, "E380", {"start": v(-3.3, 1.54) * mm, "end": v(-3.27, 1.54) * mm});
            skLineSegment(sketch, "E381", {"start": v(-3.27, 1.54) * mm, "end": v(-3.24, 1.55) * mm});
            skLineSegment(sketch, "E382", {"start": v(-3.24, 1.55) * mm, "end": v(-3.22, 1.57) * mm});
            skLineSegment(sketch, "E383", {"start": v(-3.22, 1.57) * mm, "end": v(-3.21, 1.59) * mm});
            skLineSegment(sketch, "E384", {"start": v(-3.21, 1.59) * mm, "end": v(-3.2, 1.6) * mm});
            skLineSegment(sketch, "E385", {"start": v(-3.2, 1.6) * mm, "end": v(-3.12, 1.94) * mm});
            skLineSegment(sketch, "E386", {"start": v(-3.12, 1.94) * mm, "end": v(-3.12, 1.95) * mm});
            skLineSegment(sketch, "E387", {"start": v(-3.12, 1.95) * mm, "end": v(-3.11, 1.97) * mm});
            skLineSegment(sketch, "E388", {"start": v(-3.11, 1.97) * mm, "end": v(-3.12, 2) * mm});
            skLineSegment(sketch, "E389", {"start": v(-3.12, 2) * mm, "end": v(-3.13, 2) * mm});
            skLineSegment(sketch, "E390", {"start": v(-3.13, 2) * mm, "end": v(-3.13, 2) * mm});
            skLineSegment(sketch, "E391", {"start": v(-3.13, 2) * mm, "end": v(-3.14, 2.02) * mm});
            skLineSegment(sketch, "E392", {"start": v(-3.14, 2.02) * mm, "end": v(-3.17, 2.03) * mm});
            skLineSegment(sketch, "E393", {"start": v(-3.17, 2.03) * mm, "end": v(-3.17, 2.03) * mm});
            skLineSegment(sketch, "E394", {"start": v(-3.17, 2.03) * mm, "end": v(-3.52, 2.13) * mm});
            skLineSegment(sketch, "E395", {"start": v(-3.52, 2.13) * mm, "end": v(-3.53, 2.13) * mm});
            skLineSegment(sketch, "E396", {"start": v(-3.53, 2.13) * mm, "end": v(-3.55, 2.13) * mm});
            skLineSegment(sketch, "E397", {"start": v(-3.55, 2.13) * mm, "end": v(-3.57, 2.12) * mm});
            skLineSegment(sketch, "E398", {"start": v(-3.57, 2.12) * mm, "end": v(-3.6, 2.1) * mm});
            skLineSegment(sketch, "E399", {"start": v(-3.6, 2.1) * mm, "end": v(-3.6, 2.08) * mm});
            skLineSegment(sketch, "E400", {"start": v(-3.6, 2.08) * mm, "end": v(-3.6, 2.08) * mm});
            skLineSegment(sketch, "E401", {"start": v(-3.77, 1.9) * mm, "end": v(-3.77, 1.89) * mm});
            skLineSegment(sketch, "E402", {"start": v(-3.77, 1.89) * mm, "end": v(-3.77, 1.86) * mm});
            skLineSegment(sketch, "E403", {"start": v(-3.77, 1.86) * mm, "end": v(-3.76, 1.84) * mm});
            skLineSegment(sketch, "E404", {"start": v(-3.76, 1.84) * mm, "end": v(-3.74, 1.82) * mm});
            skLineSegment(sketch, "E405", {"start": v(-3.74, 1.82) * mm, "end": v(-3.72, 1.8) * mm});
            skLineSegment(sketch, "E406", {"start": v(-3.72, 1.8) * mm, "end": v(-3.72, 1.8) * mm});
            skLineSegment(sketch, "E407", {"start": v(-3.72, 1.8) * mm, "end": v(-3.54, 1.76) * mm});
            skLineSegment(sketch, "E408", {"start": v(-3.54, 1.76) * mm, "end": v(-3.59, 1.58) * mm});
            skLineSegment(sketch, "E409", {"start": v(-3.59, 1.58) * mm, "end": v(-3.6, 1.58) * mm});
            skLineSegment(sketch, "E410", {"start": v(-3.6, 1.58) * mm, "end": v(-3.6, 1.56) * mm});
            skLineSegment(sketch, "E411", {"start": v(-3.6, 1.56) * mm, "end": v(-3.58, 1.53) * mm});
            skLineSegment(sketch, "E412", {"start": v(-3.58, 1.53) * mm, "end": v(-3.56, 1.5) * mm});
            skLineSegment(sketch, "E413", {"start": v(-3.56, 1.5) * mm, "end": v(-3.54, 1.5) * mm});
            skLineSegment(sketch, "E414", {"start": v(-3.54, 1.5) * mm, "end": v(-3.54, 1.5) * mm});
            skLineSegment(sketch, "E415", {"start": v(-3.54, 1.5) * mm, "end": v(-3.53, 1.5) * mm});
            skLineSegment(sketch, "E416", {"start": v(-3.53, 1.5) * mm, "end": v(-3.5, 1.5) * mm});
            skLineSegment(sketch, "E417", {"start": v(-3.5, 1.5) * mm, "end": v(-3.48, 1.5) * mm});
            skLineSegment(sketch, "E418", {"start": v(-3.48, 1.5) * mm, "end": v(-3.46, 1.52) * mm});
            skLineSegment(sketch, "E419", {"start": v(-3.46, 1.52) * mm, "end": v(-3.45, 1.54) * mm});
            skLineSegment(sketch, "E420", {"start": v(-3.45, 1.54) * mm, "end": v(-3.45, 1.55) * mm});
            skLineSegment(sketch, "E421", {"start": v(-3.45, 1.55) * mm, "end": v(-3.38, 1.79) * mm});
            skLineSegment(sketch, "E422", {"start": v(-3.38, 1.79) * mm, "end": v(-3.38, 1.8) * mm});
            skLineSegment(sketch, "E423", {"start": v(-3.38, 1.8) * mm, "end": v(-3.38, 1.82) * mm});
            skLineSegment(sketch, "E424", {"start": v(-3.38, 1.82) * mm, "end": v(-3.4, 1.84) * mm});
            skLineSegment(sketch, "E425", {"start": v(-3.4, 1.84) * mm, "end": v(-3.4, 1.84) * mm});
            skLineSegment(sketch, "E426", {"start": v(-3.4, 1.84) * mm, "end": v(-3.4, 1.85) * mm});
            skLineSegment(sketch, "E427", {"start": v(-3.4, 1.85) * mm, "end": v(-3.41, 1.87) * mm});
            skLineSegment(sketch, "E428", {"start": v(-3.41, 1.87) * mm, "end": v(-3.43, 1.88) * mm});
            skLineSegment(sketch, "E429", {"start": v(-3.43, 1.88) * mm, "end": v(-3.44, 1.88) * mm});
            skLineSegment(sketch, "E430", {"start": v(-3.44, 1.88) * mm, "end": v(-3.68, 1.94) * mm});
            skLineSegment(sketch, "E431", {"start": v(-3.68, 1.94) * mm, "end": v(-3.68, 1.95) * mm});
            skLineSegment(sketch, "E432", {"start": v(-3.68, 1.95) * mm, "end": v(-3.7, 1.95) * mm});
            skLineSegment(sketch, "E433", {"start": v(-3.7, 1.95) * mm, "end": v(-3.73, 1.94) * mm});
            skLineSegment(sketch, "E434", {"start": v(-3.73, 1.94) * mm, "end": v(-3.75, 1.92) * mm});
            skLineSegment(sketch, "E435", {"start": v(-3.75, 1.92) * mm, "end": v(-3.77, 1.9) * mm});
            skLineSegment(sketch, "E436", {"start": v(-3.77, 1.9) * mm, "end": v(-3.77, 1.9) * mm});
            skLineSegment(sketch, "E437", {"start": v(-2.42, 2.76) * mm, "end": v(-2.4, 2.76) * mm});
            skLineSegment(sketch, "E438", {"start": v(-2.4, 2.76) * mm, "end": v(-2.39, 2.75) * mm});
            skLineSegment(sketch, "E439", {"start": v(-2.39, 2.75) * mm, "end": v(-2.37, 2.73) * mm});
            skLineSegment(sketch, "E440", {"start": v(-2.37, 2.73) * mm, "end": v(-2.36, 2.7) * mm});
            skLineSegment(sketch, "E441", {"start": v(-2.36, 2.7) * mm, "end": v(-2.36, 2.68) * mm});
            skLineSegment(sketch, "E442", {"start": v(-2.36, 2.68) * mm, "end": v(-2.36, 2.68) * mm});
            skLineSegment(sketch, "E443", {"start": v(-2.36, 2.68) * mm, "end": v(-2.44, 2.4) * mm});
            skLineSegment(sketch, "E444", {"start": v(-2.44, 2.4) * mm, "end": v(-2.16, 2.32) * mm});
            skLineSegment(sketch, "E445", {"start": v(-2.16, 2.32) * mm, "end": v(-2.15, 2.32) * mm});
            skLineSegment(sketch, "E446", {"start": v(-2.15, 2.32) * mm, "end": v(-2.13, 2.3) * mm});
            skLineSegment(sketch, "E447", {"start": v(-2.13, 2.3) * mm, "end": v(-2.11, 2.29) * mm});
            skLineSegment(sketch, "E448", {"start": v(-2.11, 2.29) * mm, "end": v(-2.1, 2.26) * mm});
            skLineSegment(sketch, "E449", {"start": v(-2.1, 2.26) * mm, "end": v(-2.1, 2.24) * mm});
            skLineSegment(sketch, "E450", {"start": v(-2.1, 2.24) * mm, "end": v(-2.1, 2.23) * mm});
            skLineSegment(sketch, "E451", {"start": v(-2.1, 2.23) * mm, "end": v(-2.1, 2.22) * mm});
            skLineSegment(sketch, "E452", {"start": v(-2.1, 2.22) * mm, "end": v(-2.12, 2.2) * mm});
            skLineSegment(sketch, "E453", {"start": v(-2.12, 2.2) * mm, "end": v(-2.14, 2.19) * mm});
            skLineSegment(sketch, "E454", {"start": v(-2.14, 2.19) * mm, "end": v(-2.17, 2.18) * mm});
            skLineSegment(sketch, "E455", {"start": v(-2.17, 2.18) * mm, "end": v(-2.19, 2.18) * mm});
            skLineSegment(sketch, "E456", {"start": v(-2.19, 2.18) * mm, "end": v(-2.2, 2.18) * mm});
            skLineSegment(sketch, "E457", {"start": v(-2.2, 2.18) * mm, "end": v(-2.54, 2.27) * mm});
            skLineSegment(sketch, "E458", {"start": v(-2.54, 2.27) * mm, "end": v(-2.55, 2.27) * mm});
            skLineSegment(sketch, "E459", {"start": v(-2.55, 2.27) * mm, "end": v(-2.57, 2.29) * mm});
            skLineSegment(sketch, "E460", {"start": v(-2.57, 2.29) * mm, "end": v(-2.59, 2.3) * mm});
            skLineSegment(sketch, "E461", {"start": v(-2.59, 2.3) * mm, "end": v(-2.59, 2.3) * mm});
            skLineSegment(sketch, "E462", {"start": v(-2.59, 2.3) * mm, "end": v(-2.6, 2.31) * mm});
            skLineSegment(sketch, "E463", {"start": v(-2.6, 2.31) * mm, "end": v(-2.6, 2.34) * mm});
            skLineSegment(sketch, "E464", {"start": v(-2.6, 2.34) * mm, "end": v(-2.6, 2.36) * mm});
            skLineSegment(sketch, "E465", {"start": v(-2.6, 2.36) * mm, "end": v(-2.6, 2.37) * mm});
            skLineSegment(sketch, "E466", {"start": v(-2.6, 2.37) * mm, "end": v(-2.5, 2.71) * mm});
            skLineSegment(sketch, "E467", {"start": v(-2.5, 2.71) * mm, "end": v(-2.5, 2.72) * mm});
            skLineSegment(sketch, "E468", {"start": v(-2.5, 2.72) * mm, "end": v(-2.5, 2.74) * mm});
            skLineSegment(sketch, "E469", {"start": v(-2.5, 2.74) * mm, "end": v(-2.47, 2.76) * mm});
            skLineSegment(sketch, "E470", {"start": v(-2.47, 2.76) * mm, "end": v(-2.44, 2.77) * mm});
            skLineSegment(sketch, "E471", {"start": v(-2.44, 2.77) * mm, "end": v(-2.42, 2.77) * mm});
            skLineSegment(sketch, "E472", {"start": v(-2.42, 2.77) * mm, "end": v(-2.42, 2.76) * mm});
            skLineSegment(sketch, "E473", {"start": v(-2.18, 2.81) * mm, "end": v(-2.17, 2.8) * mm});
            skLineSegment(sketch, "E474", {"start": v(-2.17, 2.8) * mm, "end": v(-2.15, 2.8) * mm});
            skLineSegment(sketch, "E475", {"start": v(-2.15, 2.8) * mm, "end": v(-2.13, 2.78) * mm});
            skLineSegment(sketch, "E476", {"start": v(-2.13, 2.78) * mm, "end": v(-2.12, 2.75) * mm});
            skLineSegment(sketch, "E477", {"start": v(-2.12, 2.75) * mm, "end": v(-2.12, 2.73) * mm});
            skLineSegment(sketch, "E478", {"start": v(-2.12, 2.73) * mm, "end": v(-2.13, 2.72) * mm});
            skLineSegment(sketch, "E479", {"start": v(-2.13, 2.72) * mm, "end": v(-2.17, 2.55) * mm});
            skLineSegment(sketch, "E480", {"start": v(-2.17, 2.55) * mm, "end": v(-2, 2.5) * mm});
            skLineSegment(sketch, "E481", {"start": v(-2, 2.5) * mm, "end": v(-2, 2.5) * mm});
            skLineSegment(sketch, "E482", {"start": v(-2, 2.5) * mm, "end": v(-1.97, 2.49) * mm});
            skLineSegment(sketch, "E483", {"start": v(-1.97, 2.49) * mm, "end": v(-1.95, 2.47) * mm});
            skLineSegment(sketch, "E484", {"start": v(-1.95, 2.47) * mm, "end": v(-1.95, 2.44) * mm});
            skLineSegment(sketch, "E485", {"start": v(-1.95, 2.44) * mm, "end": v(-1.95, 2.42) * mm});
            skLineSegment(sketch, "E486", {"start": v(-1.95, 2.42) * mm, "end": v(-1.95, 2.41) * mm});
            skLineSegment(sketch, "E487", {"start": v(-1.95, 2.41) * mm, "end": v(-1.95, 2.4) * mm});
            skLineSegment(sketch, "E488", {"start": v(-1.95, 2.4) * mm, "end": v(-1.96, 2.39) * mm});
            skLineSegment(sketch, "E489", {"start": v(-1.96, 2.39) * mm, "end": v(-1.98, 2.37) * mm});
            skLineSegment(sketch, "E490", {"start": v(-1.98, 2.37) * mm, "end": v(-2, 2.36) * mm});
            skLineSegment(sketch, "E491", {"start": v(-2, 2.36) * mm, "end": v(-2.03, 2.36) * mm});
            skLineSegment(sketch, "E492", {"start": v(-2.03, 2.36) * mm, "end": v(-2.04, 2.36) * mm});
            skLineSegment(sketch, "E493", {"start": v(-2.04, 2.36) * mm, "end": v(-2.28, 2.43) * mm});
            skLineSegment(sketch, "E494", {"start": v(-2.28, 2.43) * mm, "end": v(-2.28, 2.43) * mm});
            skLineSegment(sketch, "E495", {"start": v(-2.28, 2.43) * mm, "end": v(-2.3, 2.44) * mm});
            skLineSegment(sketch, "E496", {"start": v(-2.3, 2.44) * mm, "end": v(-2.32, 2.46) * mm});
            skLineSegment(sketch, "E497", {"start": v(-2.32, 2.46) * mm, "end": v(-2.32, 2.46) * mm});
            skLineSegment(sketch, "E498", {"start": v(-2.32, 2.46) * mm, "end": v(-2.32, 2.47) * mm});
            skLineSegment(sketch, "E499", {"start": v(-2.32, 2.47) * mm, "end": v(-2.33, 2.49) * mm});
            skLineSegment(sketch, "E500", {"start": v(-2.33, 2.49) * mm, "end": v(-2.33, 2.52) * mm});
            skLineSegment(sketch, "E501", {"start": v(-2.33, 2.52) * mm, "end": v(-2.33, 2.52) * mm});
            skLineSegment(sketch, "E502", {"start": v(-2.33, 2.52) * mm, "end": v(-2.27, 2.76) * mm});
            skLineSegment(sketch, "E503", {"start": v(-2.27, 2.76) * mm, "end": v(-2.26, 2.77) * mm});
            skLineSegment(sketch, "E504", {"start": v(-2.26, 2.77) * mm, "end": v(-2.25, 2.79) * mm});
            skLineSegment(sketch, "E505", {"start": v(-2.25, 2.79) * mm, "end": v(-2.23, 2.8) * mm});
            skLineSegment(sketch, "E506", {"start": v(-2.23, 2.8) * mm, "end": v(-2.2, 2.81) * mm});
            skLineSegment(sketch, "E507", {"start": v(-2.2, 2.81) * mm, "end": v(-2.18, 2.81) * mm});
            skLineSegment(sketch, "E508", {"start": v(-2.18, 2.81) * mm, "end": v(-2.18, 2.81) * mm});
            skLineSegment(sketch, "E509", {"start": v(2.93, -4.22) * mm, "end": v(2.93, -2.3) * mm});
            skLineSegment(sketch, "E510", {"start": v(2.93, -2.3) * mm, "end": v(2.93, -2.3) * mm});
            skLineSegment(sketch, "E511", {"start": v(2.93, -2.3) * mm, "end": v(2.92, -2.28) * mm});
            skLineSegment(sketch, "E512", {"start": v(2.92, -2.28) * mm, "end": v(2.9, -2.25) * mm});
            skLineSegment(sketch, "E513", {"start": v(2.9, -2.25) * mm, "end": v(2.89, -2.24) * mm});
            skLineSegment(sketch, "E514", {"start": v(2.89, -2.24) * mm, "end": v(2.86, -2.23) * mm});
            skLineSegment(sketch, "E515", {"start": v(2.86, -2.23) * mm, "end": v(2.86, -2.23) * mm});
            skLineSegment(sketch, "E516", {"start": v(2.86, -2.23) * mm, "end": v(2.85, -2.23) * mm});
            skLineSegment(sketch, "E517", {"start": v(2.85, -2.23) * mm, "end": v(2.83, -2.24) * mm});
            skLineSegment(sketch, "E518", {"start": v(2.83, -2.24) * mm, "end": v(2.8, -2.25) * mm});
            skLineSegment(sketch, "E519", {"start": v(2.8, -2.25) * mm, "end": v(2.79, -2.28) * mm});
            skLineSegment(sketch, "E520", {"start": v(2.79, -2.28) * mm, "end": v(2.78, -2.3) * mm});
            skLineSegment(sketch, "E521", {"start": v(2.78, -2.3) * mm, "end": v(2.78, -2.3) * mm});
            skLineSegment(sketch, "E522", {"start": v(2.78, -2.3) * mm, "end": v(2.78, -4.22) * mm});
            skLineSegment(sketch, "E523", {"start": v(2.78, -4.22) * mm, "end": v(2.78, -4.23) * mm});
            skLineSegment(sketch, "E524", {"start": v(2.78, -4.23) * mm, "end": v(2.79, -4.25) * mm});
            skLineSegment(sketch, "E525", {"start": v(2.79, -4.25) * mm, "end": v(2.8, -4.27) * mm});
            skLineSegment(sketch, "E526", {"start": v(2.8, -4.27) * mm, "end": v(2.83, -4.29) * mm});
            skLineSegment(sketch, "E527", {"start": v(2.83, -4.29) * mm, "end": v(2.85, -4.3) * mm});
            skLineSegment(sketch, "E528", {"start": v(2.85, -4.3) * mm, "end": v(2.86, -4.3) * mm});
            skLineSegment(sketch, "E529", {"start": v(2.86, -4.3) * mm, "end": v(2.86, -4.3) * mm});
            skLineSegment(sketch, "E530", {"start": v(2.86, -4.3) * mm, "end": v(2.89, -4.29) * mm});
            skLineSegment(sketch, "E531", {"start": v(2.89, -4.29) * mm, "end": v(2.9, -4.27) * mm});
            skLineSegment(sketch, "E532", {"start": v(2.9, -4.27) * mm, "end": v(2.92, -4.25) * mm});
            skLineSegment(sketch, "E533", {"start": v(2.92, -4.25) * mm, "end": v(2.93, -4.23) * mm});
            skLineSegment(sketch, "E534", {"start": v(2.93, -4.23) * mm, "end": v(2.93, -4.22) * mm});
            skLineSegment(sketch, "E535", {"start": v(3.17, -2.43) * mm, "end": v(3.16, -2.42) * mm});
            skLineSegment(sketch, "E536", {"start": v(3.16, -2.42) * mm, "end": v(3.14, -2.4) * mm});
            skLineSegment(sketch, "E537", {"start": v(3.14, -2.4) * mm, "end": v(3.11, -2.4) * mm});
            skLineSegment(sketch, "E538", {"start": v(3.11, -2.4) * mm, "end": v(3.09, -2.4) * mm});
            skLineSegment(sketch, "E539", {"start": v(3.09, -2.4) * mm, "end": v(3.07, -2.42) * mm});
            skLineSegment(sketch, "E540", {"start": v(3.07, -2.42) * mm, "end": v(3.06, -2.43) * mm});
            skLineSegment(sketch, "E541", {"start": v(3.06, -2.43) * mm, "end": v(2.86, -2.63) * mm});
            skLineSegment(sketch, "E542", {"start": v(2.86, -2.63) * mm, "end": v(2.65, -2.43) * mm});
            skLineSegment(sketch, "E543", {"start": v(2.65, -2.43) * mm, "end": v(2.65, -2.42) * mm});
            skLineSegment(sketch, "E544", {"start": v(2.65, -2.42) * mm, "end": v(2.63, -2.4) * mm});
            skLineSegment(sketch, "E545", {"start": v(2.63, -2.4) * mm, "end": v(2.6, -2.4) * mm});
            skLineSegment(sketch, "E546", {"start": v(2.6, -2.4) * mm, "end": v(2.57, -2.4) * mm});
            skLineSegment(sketch, "E547", {"start": v(2.57, -2.4) * mm, "end": v(2.55, -2.42) * mm});
            skLineSegment(sketch, "E548", {"start": v(2.55, -2.42) * mm, "end": v(2.55, -2.43) * mm});
            skLineSegment(sketch, "E549", {"start": v(2.55, -2.43) * mm, "end": v(2.54, -2.43) * mm});
            skLineSegment(sketch, "E550", {"start": v(2.54, -2.43) * mm, "end": v(2.53, -2.45) * mm});
            skLineSegment(sketch, "E551", {"start": v(2.53, -2.45) * mm, "end": v(2.53, -2.48) * mm});
            skLineSegment(sketch, "E552", {"start": v(2.53, -2.48) * mm, "end": v(2.53, -2.5) * mm});
            skLineSegment(sketch, "E553", {"start": v(2.53, -2.5) * mm, "end": v(2.54, -2.52) * mm});
            skLineSegment(sketch, "E554", {"start": v(2.54, -2.52) * mm, "end": v(2.55, -2.53) * mm});
            skLineSegment(sketch, "E555", {"start": v(2.55, -2.53) * mm, "end": v(2.8, -2.78) * mm});
            skLineSegment(sketch, "E556", {"start": v(2.8, -2.78) * mm, "end": v(2.8, -2.79) * mm});
            skLineSegment(sketch, "E557", {"start": v(2.8, -2.79) * mm, "end": v(2.83, -2.8) * mm});
            skLineSegment(sketch, "E558", {"start": v(2.83, -2.8) * mm, "end": v(2.85, -2.8) * mm});
            skLineSegment(sketch, "E559", {"start": v(2.85, -2.8) * mm, "end": v(2.86, -2.8) * mm});
            skLineSegment(sketch, "E560", {"start": v(2.86, -2.8) * mm, "end": v(2.86, -2.8) * mm});
            skLineSegment(sketch, "E561", {"start": v(2.86, -2.8) * mm, "end": v(2.89, -2.8) * mm});
            skLineSegment(sketch, "E562", {"start": v(2.89, -2.8) * mm, "end": v(2.9, -2.79) * mm});
            skLineSegment(sketch, "E563", {"start": v(2.9, -2.79) * mm, "end": v(2.91, -2.78) * mm});
            skLineSegment(sketch, "E564", {"start": v(2.91, -2.78) * mm, "end": v(3.17, -2.53) * mm});
            skLineSegment(sketch, "E565", {"start": v(3.17, -2.53) * mm, "end": v(3.17, -2.52) * mm});
            skLineSegment(sketch, "E566", {"start": v(3.17, -2.52) * mm, "end": v(3.18, -2.5) * mm});
            skLineSegment(sketch, "E567", {"start": v(3.18, -2.5) * mm, "end": v(3.19, -2.48) * mm});
            skLineSegment(sketch, "E568", {"start": v(3.19, -2.48) * mm, "end": v(3.18, -2.45) * mm});
            skLineSegment(sketch, "E569", {"start": v(3.18, -2.45) * mm, "end": v(3.17, -2.43) * mm});
            skLineSegment(sketch, "E570", {"start": v(3.17, -2.43) * mm, "end": v(3.17, -2.43) * mm});
            skLineSegment(sketch, "E571", {"start": v(2.55, -4.1) * mm, "end": v(2.55, -4.1) * mm});
            skLineSegment(sketch, "E572", {"start": v(2.55, -4.1) * mm, "end": v(2.57, -4.12) * mm});
            skLineSegment(sketch, "E573", {"start": v(2.57, -4.12) * mm, "end": v(2.6, -4.12) * mm});
            skLineSegment(sketch, "E574", {"start": v(2.6, -4.12) * mm, "end": v(2.63, -4.12) * mm});
            skLineSegment(sketch, "E575", {"start": v(2.63, -4.12) * mm, "end": v(2.65, -4.1) * mm});
            skLineSegment(sketch, "E576", {"start": v(2.65, -4.1) * mm, "end": v(2.65, -4.1) * mm});
            skLineSegment(sketch, "E577", {"start": v(2.65, -4.1) * mm, "end": v(2.86, -3.9) * mm});
            skLineSegment(sketch, "E578", {"start": v(2.86, -3.9) * mm, "end": v(3.06, -4.1) * mm});
            skLineSegment(sketch, "E579", {"start": v(3.06, -4.1) * mm, "end": v(3.07, -4.1) * mm});
            skLineSegment(sketch, "E580", {"start": v(3.07, -4.1) * mm, "end": v(3.09, -4.12) * mm});
            skLineSegment(sketch, "E581", {"start": v(3.09, -4.12) * mm, "end": v(3.11, -4.12) * mm});
            skLineSegment(sketch, "E582", {"start": v(3.11, -4.12) * mm, "end": v(3.14, -4.12) * mm});
            skLineSegment(sketch, "E583", {"start": v(3.14, -4.12) * mm, "end": v(3.16, -4.1) * mm});
            skLineSegment(sketch, "E584", {"start": v(3.16, -4.1) * mm, "end": v(3.17, -4.1) * mm});
            skLineSegment(sketch, "E585", {"start": v(3.17, -4.1) * mm, "end": v(3.17, -4.1) * mm});
            skLineSegment(sketch, "E586", {"start": v(3.17, -4.1) * mm, "end": v(3.18, -4.08) * mm});
            skLineSegment(sketch, "E587", {"start": v(3.18, -4.08) * mm, "end": v(3.19, -4.05) * mm});
            skLineSegment(sketch, "E588", {"start": v(3.19, -4.05) * mm, "end": v(3.18, -4.02) * mm});
            skLineSegment(sketch, "E589", {"start": v(3.18, -4.02) * mm, "end": v(3.17, -4) * mm});
            skLineSegment(sketch, "E590", {"start": v(3.17, -4) * mm, "end": v(3.17, -4) * mm});
            skLineSegment(sketch, "E591", {"start": v(3.17, -4) * mm, "end": v(2.91, -3.75) * mm});
            skLineSegment(sketch, "E592", {"start": v(2.91, -3.75) * mm, "end": v(2.9, -3.74) * mm});
            skLineSegment(sketch, "E593", {"start": v(2.9, -3.74) * mm, "end": v(2.89, -3.73) * mm});
            skLineSegment(sketch, "E594", {"start": v(2.89, -3.73) * mm, "end": v(2.86, -3.72) * mm});
            skLineSegment(sketch, "E595", {"start": v(2.86, -3.72) * mm, "end": v(2.86, -3.72) * mm});
            skLineSegment(sketch, "E596", {"start": v(2.86, -3.72) * mm, "end": v(2.85, -3.72) * mm});
            skLineSegment(sketch, "E597", {"start": v(2.85, -3.72) * mm, "end": v(2.83, -3.73) * mm});
            skLineSegment(sketch, "E598", {"start": v(2.83, -3.73) * mm, "end": v(2.8, -3.74) * mm});
            skLineSegment(sketch, "E599", {"start": v(2.8, -3.74) * mm, "end": v(2.8, -3.75) * mm});
            skLineSegment(sketch, "E600", {"start": v(2.8, -3.75) * mm, "end": v(2.55, -4) * mm});
            skLineSegment(sketch, "E601", {"start": v(2.55, -4) * mm, "end": v(2.54, -4) * mm});
            skLineSegment(sketch, "E602", {"start": v(2.54, -4) * mm, "end": v(2.53, -4.02) * mm});
            skLineSegment(sketch, "E603", {"start": v(2.53, -4.02) * mm, "end": v(2.53, -4.05) * mm});
            skLineSegment(sketch, "E604", {"start": v(2.53, -4.05) * mm, "end": v(2.53, -4.08) * mm});
            skLineSegment(sketch, "E605", {"start": v(2.53, -4.08) * mm, "end": v(2.54, -4.1) * mm});
            skLineSegment(sketch, "E606", {"start": v(2.54, -4.1) * mm, "end": v(2.55, -4.1) * mm});
            skLineSegment(sketch, "E607", {"start": v(3.72, -3.68) * mm, "end": v(2.06, -2.72) * mm});
            skLineSegment(sketch, "E608", {"start": v(2.06, -2.72) * mm, "end": v(2.06, -2.72) * mm});
            skLineSegment(sketch, "E609", {"start": v(2.06, -2.72) * mm, "end": v(2.04, -2.71) * mm});
            skLineSegment(sketch, "E610", {"start": v(2.04, -2.71) * mm, "end": v(2, -2.71) * mm});
            skLineSegment(sketch, "E611", {"start": v(2, -2.71) * mm, "end": v(1.98, -2.73) * mm});
            skLineSegment(sketch, "E612", {"start": v(1.98, -2.73) * mm, "end": v(1.97, -2.74) * mm});
            skLineSegment(sketch, "E613", {"start": v(1.97, -2.74) * mm, "end": v(1.96, -2.75) * mm});
            skLineSegment(sketch, "E614", {"start": v(1.96, -2.75) * mm, "end": v(1.96, -2.75) * mm});
            skLineSegment(sketch, "E615", {"start": v(1.96, -2.75) * mm, "end": v(1.95, -2.78) * mm});
            skLineSegment(sketch, "E616", {"start": v(1.95, -2.78) * mm, "end": v(1.96, -2.8) * mm});
            skLineSegment(sketch, "E617", {"start": v(1.96, -2.8) * mm, "end": v(1.97, -2.83) * mm});
            skLineSegment(sketch, "E618", {"start": v(1.97, -2.83) * mm, "end": v(1.98, -2.84) * mm});
            skLineSegment(sketch, "E619", {"start": v(1.98, -2.84) * mm, "end": v(2, -2.85) * mm});
            skLineSegment(sketch, "E620", {"start": v(2, -2.85) * mm, "end": v(3.65, -3.8) * mm});
            skLineSegment(sketch, "E621", {"start": v(3.65, -3.8) * mm, "end": v(3.66, -3.8) * mm});
            skLineSegment(sketch, "E622", {"start": v(3.66, -3.8) * mm, "end": v(3.68, -3.82) * mm});
            skLineSegment(sketch, "E623", {"start": v(3.68, -3.82) * mm, "end": v(3.7, -3.81) * mm});
            skLineSegment(sketch, "E624", {"start": v(3.7, -3.81) * mm, "end": v(3.73, -3.8) * mm});
            skLineSegment(sketch, "E625", {"start": v(3.73, -3.8) * mm, "end": v(3.75, -3.79) * mm});
            skLineSegment(sketch, "E626", {"start": v(3.75, -3.79) * mm, "end": v(3.75, -3.78) * mm});
            skLineSegment(sketch, "E627", {"start": v(3.75, -3.78) * mm, "end": v(3.75, -3.77) * mm});
            skLineSegment(sketch, "E628", {"start": v(3.75, -3.77) * mm, "end": v(3.76, -3.75) * mm});
            skLineSegment(sketch, "E629", {"start": v(3.76, -3.75) * mm, "end": v(3.76, -3.72) * mm});
            skLineSegment(sketch, "E630", {"start": v(3.76, -3.72) * mm, "end": v(3.74, -3.7) * mm});
            skLineSegment(sketch, "E631", {"start": v(3.74, -3.7) * mm, "end": v(3.73, -3.68) * mm});
            skLineSegment(sketch, "E632", {"start": v(3.73, -3.68) * mm, "end": v(3.72, -3.68) * mm});
            skLineSegment(sketch, "E633", {"start": v(2.29, -2.58) * mm, "end": v(2.28, -2.58) * mm});
            skLineSegment(sketch, "E634", {"start": v(2.28, -2.58) * mm, "end": v(2.26, -2.6) * mm});
            skLineSegment(sketch, "E635", {"start": v(2.26, -2.6) * mm, "end": v(2.24, -2.61) * mm});
            skLineSegment(sketch, "E636", {"start": v(2.24, -2.61) * mm, "end": v(2.23, -2.64) * mm});
            skLineSegment(sketch, "E637", {"start": v(2.23, -2.64) * mm, "end": v(2.23, -2.66) * mm});
            skLineSegment(sketch, "E638", {"start": v(2.23, -2.66) * mm, "end": v(2.23, -2.67) * mm});
            skLineSegment(sketch, "E639", {"start": v(2.23, -2.67) * mm, "end": v(2.3, -2.95) * mm});
            skLineSegment(sketch, "E640", {"start": v(2.3, -2.95) * mm, "end": v(2.03, -3.02) * mm});
            skLineSegment(sketch, "E641", {"start": v(2.03, -3.02) * mm, "end": v(2.02, -3.03) * mm});
            skLineSegment(sketch, "E642", {"start": v(2.02, -3.03) * mm, "end": v(2, -3.04) * mm});
            skLineSegment(sketch, "E643", {"start": v(2, -3.04) * mm, "end": v(1.98, -3.06) * mm});
            skLineSegment(sketch, "E644", {"start": v(1.98, -3.06) * mm, "end": v(1.97, -3.08) * mm});
            skLineSegment(sketch, "E645", {"start": v(1.97, -3.08) * mm, "end": v(1.97, -3.1) * mm});
            skLineSegment(sketch, "E646", {"start": v(1.97, -3.1) * mm, "end": v(1.98, -3.11) * mm});
            skLineSegment(sketch, "E647", {"start": v(1.98, -3.11) * mm, "end": v(1.98, -3.12) * mm});
            skLineSegment(sketch, "E648", {"start": v(1.98, -3.12) * mm, "end": v(1.99, -3.14) * mm});
            skLineSegment(sketch, "E649", {"start": v(1.99, -3.14) * mm, "end": v(2.01, -3.16) * mm});
            skLineSegment(sketch, "E650", {"start": v(2.01, -3.16) * mm, "end": v(2.04, -3.17) * mm});
            skLineSegment(sketch, "E651", {"start": v(2.04, -3.17) * mm, "end": v(2.06, -3.17) * mm});
            skLineSegment(sketch, "E652", {"start": v(2.06, -3.17) * mm, "end": v(2.07, -3.16) * mm});
            skLineSegment(sketch, "E653", {"start": v(2.07, -3.16) * mm, "end": v(2.41, -3.07) * mm});
            skLineSegment(sketch, "E654", {"start": v(2.41, -3.07) * mm, "end": v(2.42, -3.07) * mm});
            skLineSegment(sketch, "E655", {"start": v(2.42, -3.07) * mm, "end": v(2.44, -3.06) * mm});
            skLineSegment(sketch, "E656", {"start": v(2.44, -3.06) * mm, "end": v(2.46, -3.04) * mm});
            skLineSegment(sketch, "E657", {"start": v(2.46, -3.04) * mm, "end": v(2.46, -3.03) * mm});
            skLineSegment(sketch, "E658", {"start": v(2.46, -3.03) * mm, "end": v(2.46, -3.03) * mm});
            skLineSegment(sketch, "E659", {"start": v(2.46, -3.03) * mm, "end": v(2.47, -3) * mm});
            skLineSegment(sketch, "E660", {"start": v(2.47, -3) * mm, "end": v(2.47, -2.98) * mm});
            skLineSegment(sketch, "E661", {"start": v(2.47, -2.98) * mm, "end": v(2.47, -2.98) * mm});
            skLineSegment(sketch, "E662", {"start": v(2.47, -2.98) * mm, "end": v(2.37, -2.63) * mm});
            skLineSegment(sketch, "E663", {"start": v(2.37, -2.63) * mm, "end": v(2.37, -2.62) * mm});
            skLineSegment(sketch, "E664", {"start": v(2.37, -2.62) * mm, "end": v(2.36, -2.6) * mm});
            skLineSegment(sketch, "E665", {"start": v(2.36, -2.6) * mm, "end": v(2.34, -2.58) * mm});
            skLineSegment(sketch, "E666", {"start": v(2.34, -2.58) * mm, "end": v(2.31, -2.58) * mm});
            skLineSegment(sketch, "E667", {"start": v(2.31, -2.58) * mm, "end": v(2.3, -2.58) * mm});
            skLineSegment(sketch, "E668", {"start": v(2.3, -2.58) * mm, "end": v(2.29, -2.58) * mm});
            skLineSegment(sketch, "E669", {"start": v(3.43, -3.95) * mm, "end": v(3.44, -3.95) * mm});
            skLineSegment(sketch, "E670", {"start": v(3.44, -3.95) * mm, "end": v(3.45, -3.94) * mm});
            skLineSegment(sketch, "E671", {"start": v(3.45, -3.94) * mm, "end": v(3.47, -3.92) * mm});
            skLineSegment(sketch, "E672", {"start": v(3.47, -3.92) * mm, "end": v(3.48, -3.9) * mm});
            skLineSegment(sketch, "E673", {"start": v(3.48, -3.9) * mm, "end": v(3.48, -3.87) * mm});
            skLineSegment(sketch, "E674", {"start": v(3.48, -3.87) * mm, "end": v(3.48, -3.86) * mm});
            skLineSegment(sketch, "E675", {"start": v(3.48, -3.86) * mm, "end": v(3.4, -3.58) * mm});
            skLineSegment(sketch, "E676", {"start": v(3.4, -3.58) * mm, "end": v(3.69, -3.5) * mm});
            skLineSegment(sketch, "E677", {"start": v(3.69, -3.5) * mm, "end": v(3.7, -3.5) * mm});
            skLineSegment(sketch, "E678", {"start": v(3.7, -3.5) * mm, "end": v(3.71, -3.5) * mm});
            skLineSegment(sketch, "E679", {"start": v(3.71, -3.5) * mm, "end": v(3.73, -3.47) * mm});
            skLineSegment(sketch, "E680", {"start": v(3.73, -3.47) * mm, "end": v(3.74, -3.45) * mm});
            skLineSegment(sketch, "E681", {"start": v(3.74, -3.45) * mm, "end": v(3.74, -3.42) * mm});
            skLineSegment(sketch, "E682", {"start": v(3.74, -3.42) * mm, "end": v(3.74, -3.42) * mm});
            skLineSegment(sketch, "E683", {"start": v(3.74, -3.42) * mm, "end": v(3.74, -3.4) * mm});
            skLineSegment(sketch, "E684", {"start": v(3.74, -3.4) * mm, "end": v(3.72, -3.4) * mm});
            skLineSegment(sketch, "E685", {"start": v(3.72, -3.4) * mm, "end": v(3.7, -3.37) * mm});
            skLineSegment(sketch, "E686", {"start": v(3.7, -3.37) * mm, "end": v(3.68, -3.36) * mm});
            skLineSegment(sketch, "E687", {"start": v(3.68, -3.36) * mm, "end": v(3.66, -3.36) * mm});
            skLineSegment(sketch, "E688", {"start": v(3.66, -3.36) * mm, "end": v(3.65, -3.36) * mm});
            skLineSegment(sketch, "E689", {"start": v(3.65, -3.36) * mm, "end": v(3.3, -3.46) * mm});
            skLineSegment(sketch, "E690", {"start": v(3.3, -3.46) * mm, "end": v(3.3, -3.46) * mm});
            skLineSegment(sketch, "E691", {"start": v(3.3, -3.46) * mm, "end": v(3.27, -3.47) * mm});
            skLineSegment(sketch, "E692", {"start": v(3.27, -3.47) * mm, "end": v(3.26, -3.49) * mm});
            skLineSegment(sketch, "E693", {"start": v(3.26, -3.49) * mm, "end": v(3.26, -3.5) * mm});
            skLineSegment(sketch, "E694", {"start": v(3.26, -3.5) * mm, "end": v(3.25, -3.5) * mm});
            skLineSegment(sketch, "E695", {"start": v(3.25, -3.5) * mm, "end": v(3.25, -3.52) * mm});
            skLineSegment(sketch, "E696", {"start": v(3.25, -3.52) * mm, "end": v(3.25, -3.55) * mm});
            skLineSegment(sketch, "E697", {"start": v(3.25, -3.55) * mm, "end": v(3.25, -3.55) * mm});
            skLineSegment(sketch, "E698", {"start": v(3.25, -3.55) * mm, "end": v(3.34, -3.9) * mm});
            skLineSegment(sketch, "E699", {"start": v(3.34, -3.9) * mm, "end": v(3.34, -3.9) * mm});
            skLineSegment(sketch, "E700", {"start": v(3.34, -3.9) * mm, "end": v(3.35, -3.93) * mm});
            skLineSegment(sketch, "E701", {"start": v(3.35, -3.93) * mm, "end": v(3.37, -3.94) * mm});
            skLineSegment(sketch, "E702", {"start": v(3.37, -3.94) * mm, "end": v(3.4, -3.95) * mm});
            skLineSegment(sketch, "E703", {"start": v(3.4, -3.95) * mm, "end": v(3.42, -3.95) * mm});
            skLineSegment(sketch, "E704", {"start": v(3.42, -3.95) * mm, "end": v(3.43, -3.95) * mm});
            skLineSegment(sketch, "E705", {"start": v(3.65, -2.72) * mm, "end": v(2, -3.68) * mm});
            skLineSegment(sketch, "E706", {"start": v(2, -3.68) * mm, "end": v(1.98, -3.68) * mm});
            skLineSegment(sketch, "E707", {"start": v(1.98, -3.68) * mm, "end": v(1.97, -3.7) * mm});
            skLineSegment(sketch, "E708", {"start": v(1.97, -3.7) * mm, "end": v(1.96, -3.72) * mm});
            skLineSegment(sketch, "E709", {"start": v(1.96, -3.72) * mm, "end": v(1.95, -3.75) * mm});
            skLineSegment(sketch, "E710", {"start": v(1.95, -3.75) * mm, "end": v(1.96, -3.77) * mm});
            skLineSegment(sketch, "E711", {"start": v(1.96, -3.77) * mm, "end": v(1.96, -3.78) * mm});
            skLineSegment(sketch, "E712", {"start": v(1.96, -3.78) * mm, "end": v(1.97, -3.79) * mm});
            skLineSegment(sketch, "E713", {"start": v(1.97, -3.79) * mm, "end": v(1.98, -3.8) * mm});
            skLineSegment(sketch, "E714", {"start": v(1.98, -3.8) * mm, "end": v(2, -3.81) * mm});
            skLineSegment(sketch, "E715", {"start": v(2, -3.81) * mm, "end": v(2.04, -3.82) * mm});
            skLineSegment(sketch, "E716", {"start": v(2.04, -3.82) * mm, "end": v(2.06, -3.8) * mm});
            skLineSegment(sketch, "E717", {"start": v(2.06, -3.8) * mm, "end": v(2.06, -3.8) * mm});
            skLineSegment(sketch, "E718", {"start": v(2.06, -3.8) * mm, "end": v(3.72, -2.85) * mm});
            skLineSegment(sketch, "E719", {"start": v(3.72, -2.85) * mm, "end": v(3.73, -2.84) * mm});
            skLineSegment(sketch, "E720", {"start": v(3.73, -2.84) * mm, "end": v(3.74, -2.83) * mm});
            skLineSegment(sketch, "E721", {"start": v(3.74, -2.83) * mm, "end": v(3.76, -2.8) * mm});
            skLineSegment(sketch, "E722", {"start": v(3.76, -2.8) * mm, "end": v(3.76, -2.78) * mm});
            skLineSegment(sketch, "E723", {"start": v(3.76, -2.78) * mm, "end": v(3.75, -2.75) * mm});
            skLineSegment(sketch, "E724", {"start": v(3.75, -2.75) * mm, "end": v(3.75, -2.75) * mm});
            skLineSegment(sketch, "E725", {"start": v(3.75, -2.75) * mm, "end": v(3.75, -2.74) * mm});
            skLineSegment(sketch, "E726", {"start": v(3.75, -2.74) * mm, "end": v(3.73, -2.73) * mm});
            skLineSegment(sketch, "E727", {"start": v(3.73, -2.73) * mm, "end": v(3.7, -2.71) * mm});
            skLineSegment(sketch, "E728", {"start": v(3.7, -2.71) * mm, "end": v(3.68, -2.71) * mm});
            skLineSegment(sketch, "E729", {"start": v(3.68, -2.71) * mm, "end": v(3.66, -2.72) * mm});
            skLineSegment(sketch, "E730", {"start": v(3.66, -2.72) * mm, "end": v(3.65, -2.72) * mm});
            skLineSegment(sketch, "E731", {"start": v(1.98, -3.42) * mm, "end": v(1.97, -3.42) * mm});
            skLineSegment(sketch, "E732", {"start": v(1.97, -3.42) * mm, "end": v(1.97, -3.45) * mm});
            skLineSegment(sketch, "E733", {"start": v(1.97, -3.45) * mm, "end": v(1.98, -3.47) * mm});
            skLineSegment(sketch, "E734", {"start": v(1.98, -3.47) * mm, "end": v(2, -3.5) * mm});
            skLineSegment(sketch, "E735", {"start": v(2, -3.5) * mm, "end": v(2.02, -3.5) * mm});
            skLineSegment(sketch, "E736", {"start": v(2.02, -3.5) * mm, "end": v(2.03, -3.5) * mm});
            skLineSegment(sketch, "E737", {"start": v(2.03, -3.5) * mm, "end": v(2.3, -3.58) * mm});
            skLineSegment(sketch, "E738", {"start": v(2.3, -3.58) * mm, "end": v(2.23, -3.86) * mm});
            skLineSegment(sketch, "E739", {"start": v(2.23, -3.86) * mm, "end": v(2.23, -3.87) * mm});
            skLineSegment(sketch, "E740", {"start": v(2.23, -3.87) * mm, "end": v(2.23, -3.9) * mm});
            skLineSegment(sketch, "E741", {"start": v(2.23, -3.9) * mm, "end": v(2.24, -3.92) * mm});
            skLineSegment(sketch, "E742", {"start": v(2.24, -3.92) * mm, "end": v(2.26, -3.94) * mm});
            skLineSegment(sketch, "E743", {"start": v(2.26, -3.94) * mm, "end": v(2.28, -3.95) * mm});
            skLineSegment(sketch, "E744", {"start": v(2.28, -3.95) * mm, "end": v(2.29, -3.95) * mm});
            skLineSegment(sketch, "E745", {"start": v(2.29, -3.95) * mm, "end": v(2.3, -3.95) * mm});
            skLineSegment(sketch, "E746", {"start": v(2.3, -3.95) * mm, "end": v(2.31, -3.95) * mm});
            skLineSegment(sketch, "E747", {"start": v(2.31, -3.95) * mm, "end": v(2.34, -3.94) * mm});
            skLineSegment(sketch, "E748", {"start": v(2.34, -3.94) * mm, "end": v(2.36, -3.93) * mm});
            skLineSegment(sketch, "E749", {"start": v(2.36, -3.93) * mm, "end": v(2.37, -3.9) * mm});
            skLineSegment(sketch, "E750", {"start": v(2.37, -3.9) * mm, "end": v(2.37, -3.9) * mm});
            skLineSegment(sketch, "E751", {"start": v(2.37, -3.9) * mm, "end": v(2.47, -3.55) * mm});
            skLineSegment(sketch, "E752", {"start": v(2.47, -3.55) * mm, "end": v(2.47, -3.55) * mm});
            skLineSegment(sketch, "E753", {"start": v(2.47, -3.55) * mm, "end": v(2.47, -3.52) * mm});
            skLineSegment(sketch, "E754", {"start": v(2.47, -3.52) * mm, "end": v(2.46, -3.5) * mm});
            skLineSegment(sketch, "E755", {"start": v(2.46, -3.5) * mm, "end": v(2.46, -3.5) * mm});
            skLineSegment(sketch, "E756", {"start": v(2.46, -3.5) * mm, "end": v(2.46, -3.49) * mm});
            skLineSegment(sketch, "E757", {"start": v(2.46, -3.49) * mm, "end": v(2.44, -3.47) * mm});
            skLineSegment(sketch, "E758", {"start": v(2.44, -3.47) * mm, "end": v(2.42, -3.46) * mm});
            skLineSegment(sketch, "E759", {"start": v(2.42, -3.46) * mm, "end": v(2.41, -3.46) * mm});
            skLineSegment(sketch, "E760", {"start": v(2.41, -3.46) * mm, "end": v(2.07, -3.36) * mm});
            skLineSegment(sketch, "E761", {"start": v(2.07, -3.36) * mm, "end": v(2.06, -3.36) * mm});
            skLineSegment(sketch, "E762", {"start": v(2.06, -3.36) * mm, "end": v(2.04, -3.36) * mm});
            skLineSegment(sketch, "E763", {"start": v(2.04, -3.36) * mm, "end": v(2.01, -3.37) * mm});
            skLineSegment(sketch, "E764", {"start": v(2.01, -3.37) * mm, "end": v(1.99, -3.4) * mm});
            skLineSegment(sketch, "E765", {"start": v(1.99, -3.4) * mm, "end": v(1.98, -3.4) * mm});
            skLineSegment(sketch, "E766", {"start": v(1.98, -3.4) * mm, "end": v(1.98, -3.42) * mm});
            skLineSegment(sketch, "E767", {"start": v(3.74, -3.11) * mm, "end": v(3.74, -3.1) * mm});
            skLineSegment(sketch, "E768", {"start": v(3.74, -3.1) * mm, "end": v(3.74, -3.08) * mm});
            skLineSegment(sketch, "E769", {"start": v(3.74, -3.08) * mm, "end": v(3.73, -3.06) * mm});
            skLineSegment(sketch, "E770", {"start": v(3.73, -3.06) * mm, "end": v(3.71, -3.04) * mm});
            skLineSegment(sketch, "E771", {"start": v(3.71, -3.04) * mm, "end": v(3.7, -3.03) * mm});
            skLineSegment(sketch, "E772", {"start": v(3.7, -3.03) * mm, "end": v(3.69, -3.02) * mm});
            skLineSegment(sketch, "E773", {"start": v(3.69, -3.02) * mm, "end": v(3.4, -2.95) * mm});
            skLineSegment(sketch, "E774", {"start": v(3.4, -2.95) * mm, "end": v(3.48, -2.67) * mm});
            skLineSegment(sketch, "E775", {"start": v(3.48, -2.67) * mm, "end": v(3.48, -2.66) * mm});
            skLineSegment(sketch, "E776", {"start": v(3.48, -2.66) * mm, "end": v(3.48, -2.64) * mm});
            skLineSegment(sketch, "E777", {"start": v(3.48, -2.64) * mm, "end": v(3.47, -2.61) * mm});
            skLineSegment(sketch, "E778", {"start": v(3.47, -2.61) * mm, "end": v(3.45, -2.6) * mm});
            skLineSegment(sketch, "E779", {"start": v(3.45, -2.6) * mm, "end": v(3.44, -2.58) * mm});
            skLineSegment(sketch, "E780", {"start": v(3.44, -2.58) * mm, "end": v(3.43, -2.58) * mm});
            skLineSegment(sketch, "E781", {"start": v(3.43, -2.58) * mm, "end": v(3.42, -2.58) * mm});
            skLineSegment(sketch, "E782", {"start": v(3.42, -2.58) * mm, "end": v(3.4, -2.58) * mm});
            skLineSegment(sketch, "E783", {"start": v(3.4, -2.58) * mm, "end": v(3.37, -2.58) * mm});
            skLineSegment(sketch, "E784", {"start": v(3.37, -2.58) * mm, "end": v(3.35, -2.6) * mm});
            skLineSegment(sketch, "E785", {"start": v(3.35, -2.6) * mm, "end": v(3.34, -2.62) * mm});
            skLineSegment(sketch, "E786", {"start": v(3.34, -2.62) * mm, "end": v(3.34, -2.63) * mm});
            skLineSegment(sketch, "E787", {"start": v(3.34, -2.63) * mm, "end": v(3.25, -2.98) * mm});
            skLineSegment(sketch, "E788", {"start": v(3.25, -2.98) * mm, "end": v(3.25, -2.98) * mm});
            skLineSegment(sketch, "E789", {"start": v(3.25, -2.98) * mm, "end": v(3.25, -3) * mm});
            skLineSegment(sketch, "E790", {"start": v(3.25, -3) * mm, "end": v(3.25, -3.03) * mm});
            skLineSegment(sketch, "E791", {"start": v(3.25, -3.03) * mm, "end": v(3.26, -3.03) * mm});
            skLineSegment(sketch, "E792", {"start": v(3.26, -3.03) * mm, "end": v(3.26, -3.04) * mm});
            skLineSegment(sketch, "E793", {"start": v(3.26, -3.04) * mm, "end": v(3.27, -3.06) * mm});
            skLineSegment(sketch, "E794", {"start": v(3.27, -3.06) * mm, "end": v(3.3, -3.07) * mm});
            skLineSegment(sketch, "E795", {"start": v(3.3, -3.07) * mm, "end": v(3.3, -3.07) * mm});
            skLineSegment(sketch, "E796", {"start": v(3.3, -3.07) * mm, "end": v(3.65, -3.16) * mm});
            skLineSegment(sketch, "E797", {"start": v(3.65, -3.16) * mm, "end": v(3.66, -3.17) * mm});
            skLineSegment(sketch, "E798", {"start": v(3.66, -3.17) * mm, "end": v(3.68, -3.17) * mm});
            skLineSegment(sketch, "E799", {"start": v(3.68, -3.17) * mm, "end": v(3.7, -3.16) * mm});
            skLineSegment(sketch, "E800", {"start": v(3.7, -3.16) * mm, "end": v(3.72, -3.14) * mm});
            skLineSegment(sketch, "E801", {"start": v(3.72, -3.14) * mm, "end": v(3.74, -3.12) * mm});
            skLineSegment(sketch, "E802", {"start": v(3.74, -3.12) * mm, "end": v(3.74, -3.11) * mm});
            skLineSegment(sketch, "E803", {"start": v(2.82, -3.46) * mm, "end": v(2.8, -3.47) * mm});
            skLineSegment(sketch, "E804", {"start": v(2.8, -3.47) * mm, "end": v(2.7, -3.55) * mm});
            skLineSegment(sketch, "E805", {"start": v(2.7, -3.55) * mm, "end": v(2.7, -3.55) * mm});
            skLineSegment(sketch, "E806", {"start": v(2.7, -3.55) * mm, "end": v(2.7, -3.54) * mm});
            skLineSegment(sketch, "E807", {"start": v(2.7, -3.54) * mm, "end": v(2.7, -3.4) * mm});
            skLineSegment(sketch, "E808", {"start": v(2.7, -3.4) * mm, "end": v(2.7, -3.4) * mm});
            skLineSegment(sketch, "E809", {"start": v(2.7, -3.4) * mm, "end": v(2.7, -3.38) * mm});
            skLineSegment(sketch, "E810", {"start": v(2.7, -3.38) * mm, "end": v(2.7, -3.36) * mm});
            skLineSegment(sketch, "E811", {"start": v(2.7, -3.36) * mm, "end": v(2.68, -3.34) * mm});
            skLineSegment(sketch, "E812", {"start": v(2.68, -3.34) * mm, "end": v(2.67, -3.33) * mm});
            skLineSegment(sketch, "E813", {"start": v(2.67, -3.33) * mm, "end": v(2.67, -3.33) * mm});
            skLineSegment(sketch, "E814", {"start": v(2.67, -3.33) * mm, "end": v(2.66, -3.32) * mm});
            skLineSegment(sketch, "E815", {"start": v(2.66, -3.32) * mm, "end": v(2.54, -3.27) * mm});
            skLineSegment(sketch, "E816", {"start": v(2.54, -3.27) * mm, "end": v(2.52, -3.26) * mm});
            skLineSegment(sketch, "E817", {"start": v(2.52, -3.26) * mm, "end": v(2.54, -3.26) * mm});
            skLineSegment(sketch, "E818", {"start": v(2.54, -3.26) * mm, "end": v(2.66, -3.2) * mm});
            skLineSegment(sketch, "E819", {"start": v(2.66, -3.2) * mm, "end": v(2.67, -3.2) * mm});
            skLineSegment(sketch, "E820", {"start": v(2.67, -3.2) * mm, "end": v(2.67, -3.2) * mm});
            skLineSegment(sketch, "E821", {"start": v(2.67, -3.2) * mm, "end": v(2.68, -3.19) * mm});
            skLineSegment(sketch, "E822", {"start": v(2.68, -3.19) * mm, "end": v(2.7, -3.17) * mm});
            skLineSegment(sketch, "E823", {"start": v(2.7, -3.17) * mm, "end": v(2.7, -3.15) * mm});
            skLineSegment(sketch, "E824", {"start": v(2.7, -3.15) * mm, "end": v(2.7, -3.14) * mm});
            skLineSegment(sketch, "E825", {"start": v(2.7, -3.14) * mm, "end": v(2.7, -3.13) * mm});
            skLineSegment(sketch, "E826", {"start": v(2.7, -3.13) * mm, "end": v(2.7, -3.12) * mm});
            skLineSegment(sketch, "E827", {"start": v(2.7, -3.12) * mm, "end": v(2.7, -2.99) * mm});
            skLineSegment(sketch, "E828", {"start": v(2.7, -2.99) * mm, "end": v(2.7, -2.98) * mm});
            skLineSegment(sketch, "E829", {"start": v(2.7, -2.98) * mm, "end": v(2.7, -2.98) * mm});
            skLineSegment(sketch, "E830", {"start": v(2.7, -2.98) * mm, "end": v(2.8, -3.06) * mm});
            skLineSegment(sketch, "E831", {"start": v(2.8, -3.06) * mm, "end": v(2.82, -3.07) * mm});
            skLineSegment(sketch, "E832", {"start": v(2.82, -3.07) * mm, "end": v(2.82, -3.07) * mm});
            skLineSegment(sketch, "E833", {"start": v(2.82, -3.07) * mm, "end": v(2.85, -3.08) * mm});
            skLineSegment(sketch, "E834", {"start": v(2.85, -3.08) * mm, "end": v(2.86, -3.08) * mm});
            skLineSegment(sketch, "E835", {"start": v(2.86, -3.08) * mm, "end": v(2.86, -3.08) * mm});
            skLineSegment(sketch, "E836", {"start": v(2.86, -3.08) * mm, "end": v(2.9, -3.07) * mm});
            skLineSegment(sketch, "E837", {"start": v(2.9, -3.07) * mm, "end": v(2.9, -3.07) * mm});
            skLineSegment(sketch, "E838", {"start": v(2.9, -3.07) * mm, "end": v(2.9, -3.06) * mm});
            skLineSegment(sketch, "E839", {"start": v(2.9, -3.06) * mm, "end": v(3.01, -2.98) * mm});
            skLineSegment(sketch, "E840", {"start": v(3.01, -2.98) * mm, "end": v(3.02, -2.98) * mm});
            skLineSegment(sketch, "E841", {"start": v(3.02, -2.98) * mm, "end": v(3.02, -2.99) * mm});
            skLineSegment(sketch, "E842", {"start": v(3.02, -2.99) * mm, "end": v(3, -3.12) * mm});
            skLineSegment(sketch, "E843", {"start": v(3, -3.12) * mm, "end": v(3, -3.13) * mm});
            skLineSegment(sketch, "E844", {"start": v(3, -3.13) * mm, "end": v(3, -3.14) * mm});
            skLineSegment(sketch, "E845", {"start": v(3, -3.14) * mm, "end": v(3, -3.15) * mm});
            skLineSegment(sketch, "E846", {"start": v(3, -3.15) * mm, "end": v(3.02, -3.17) * mm});
            skLineSegment(sketch, "E847", {"start": v(3.02, -3.17) * mm, "end": v(3.03, -3.19) * mm});
            skLineSegment(sketch, "E848", {"start": v(3.03, -3.19) * mm, "end": v(3.04, -3.2) * mm});
            skLineSegment(sketch, "E849", {"start": v(3.04, -3.2) * mm, "end": v(3.05, -3.2) * mm});
            skLineSegment(sketch, "E850", {"start": v(3.05, -3.2) * mm, "end": v(3.06, -3.2) * mm});
            skLineSegment(sketch, "E851", {"start": v(3.06, -3.2) * mm, "end": v(3.18, -3.26) * mm});
            skLineSegment(sketch, "E852", {"start": v(3.18, -3.26) * mm, "end": v(3.2, -3.26) * mm});
            skLineSegment(sketch, "E853", {"start": v(3.2, -3.26) * mm, "end": v(3.18, -3.27) * mm});
            skLineSegment(sketch, "E854", {"start": v(3.18, -3.27) * mm, "end": v(3.06, -3.32) * mm});
            skLineSegment(sketch, "E855", {"start": v(3.06, -3.32) * mm, "end": v(3.05, -3.33) * mm});
            skLineSegment(sketch, "E856", {"start": v(3.05, -3.33) * mm, "end": v(3.04, -3.33) * mm});
            skLineSegment(sketch, "E857", {"start": v(3.04, -3.33) * mm, "end": v(3.03, -3.34) * mm});
            skLineSegment(sketch, "E858", {"start": v(3.03, -3.34) * mm, "end": v(3.02, -3.36) * mm});
            skLineSegment(sketch, "E859", {"start": v(3.02, -3.36) * mm, "end": v(3, -3.38) * mm});
            skLineSegment(sketch, "E860", {"start": v(3, -3.38) * mm, "end": v(3, -3.4) * mm});
            skLineSegment(sketch, "E861", {"start": v(3, -3.4) * mm, "end": v(3, -3.4) * mm});
            skLineSegment(sketch, "E862", {"start": v(3, -3.4) * mm, "end": v(3.02, -3.54) * mm});
            skLineSegment(sketch, "E863", {"start": v(3.02, -3.54) * mm, "end": v(3.02, -3.55) * mm});
            skLineSegment(sketch, "E864", {"start": v(3.02, -3.55) * mm, "end": v(3.01, -3.55) * mm});
            skLineSegment(sketch, "E865", {"start": v(3.01, -3.55) * mm, "end": v(2.9, -3.47) * mm});
            skLineSegment(sketch, "E866", {"start": v(2.9, -3.47) * mm, "end": v(2.9, -3.46) * mm});
            skLineSegment(sketch, "E867", {"start": v(2.9, -3.46) * mm, "end": v(2.9, -3.46) * mm});
            skLineSegment(sketch, "E868", {"start": v(2.9, -3.46) * mm, "end": v(2.86, -3.45) * mm});
            skLineSegment(sketch, "E869", {"start": v(2.86, -3.45) * mm, "end": v(2.82, -3.46) * mm});
            skLineSegment(sketch, "E870", {"start": v(2.82, -3.46) * mm, "end": v(2.82, -3.46) * mm});
            skLineSegment(sketch, "E871", {"start": v(3.43, -3.2) * mm, "end": v(3.4, -3.19) * mm});
            skLineSegment(sketch, "E872", {"start": v(3.4, -3.19) * mm, "end": v(3.2, -3.1) * mm});
            skLineSegment(sketch, "E873", {"start": v(3.2, -3.1) * mm, "end": v(3.17, -3.08) * mm});
            skLineSegment(sketch, "E874", {"start": v(3.17, -3.08) * mm, "end": v(3.17, -3.06) * mm});
            skLineSegment(sketch, "E875", {"start": v(3.17, -3.06) * mm, "end": v(3.2, -2.83) * mm});
            skLineSegment(sketch, "E876", {"start": v(3.2, -2.83) * mm, "end": v(3.2, -2.8) * mm});
            skLineSegment(sketch, "E877", {"start": v(3.2, -2.8) * mm, "end": v(3.2, -2.8) * mm});
            skLineSegment(sketch, "E878", {"start": v(3.2, -2.8) * mm, "end": v(3.2, -2.78) * mm});
            skLineSegment(sketch, "E879", {"start": v(3.2, -2.78) * mm, "end": v(3.2, -2.77) * mm});
            skLineSegment(sketch, "E880", {"start": v(3.2, -2.77) * mm, "end": v(3.18, -2.75) * mm});
            skLineSegment(sketch, "E881", {"start": v(3.18, -2.75) * mm, "end": v(3.16, -2.74) * mm});
            skLineSegment(sketch, "E882", {"start": v(3.16, -2.74) * mm, "end": v(3.14, -2.73) * mm});
            skLineSegment(sketch, "E883", {"start": v(3.14, -2.73) * mm, "end": v(3.12, -2.73) * mm});
            skLineSegment(sketch, "E884", {"start": v(3.12, -2.73) * mm, "end": v(3.1, -2.73) * mm});
            skLineSegment(sketch, "E885", {"start": v(3.1, -2.73) * mm, "end": v(3.09, -2.73) * mm});
            skLineSegment(sketch, "E886", {"start": v(3.09, -2.73) * mm, "end": v(3.08, -2.74) * mm});
            skLineSegment(sketch, "E887", {"start": v(3.08, -2.74) * mm, "end": v(3.06, -2.75) * mm});
            skLineSegment(sketch, "E888", {"start": v(3.06, -2.75) * mm, "end": v(2.88, -2.89) * mm});
            skLineSegment(sketch, "E889", {"start": v(2.88, -2.89) * mm, "end": v(2.86, -2.9) * mm});
            skLineSegment(sketch, "E890", {"start": v(2.86, -2.9) * mm, "end": v(2.84, -2.89) * mm});
            skLineSegment(sketch, "E891", {"start": v(2.84, -2.89) * mm, "end": v(2.65, -2.75) * mm});
            skLineSegment(sketch, "E892", {"start": v(2.65, -2.75) * mm, "end": v(2.63, -2.74) * mm});
            skLineSegment(sketch, "E893", {"start": v(2.63, -2.74) * mm, "end": v(2.63, -2.73) * mm});
            skLineSegment(sketch, "E894", {"start": v(2.63, -2.73) * mm, "end": v(2.61, -2.73) * mm});
            skLineSegment(sketch, "E895", {"start": v(2.61, -2.73) * mm, "end": v(2.6, -2.73) * mm});
            skLineSegment(sketch, "E896", {"start": v(2.6, -2.73) * mm, "end": v(2.57, -2.73) * mm});
            skLineSegment(sketch, "E897", {"start": v(2.57, -2.73) * mm, "end": v(2.55, -2.74) * mm});
            skLineSegment(sketch, "E898", {"start": v(2.55, -2.74) * mm, "end": v(2.54, -2.75) * mm});
            skLineSegment(sketch, "E899", {"start": v(2.54, -2.75) * mm, "end": v(2.52, -2.77) * mm});
            skLineSegment(sketch, "E900", {"start": v(2.52, -2.77) * mm, "end": v(2.51, -2.78) * mm});
            skLineSegment(sketch, "E901", {"start": v(2.51, -2.78) * mm, "end": v(2.51, -2.8) * mm});
            skLineSegment(sketch, "E902", {"start": v(2.51, -2.8) * mm, "end": v(2.51, -2.8) * mm});
            skLineSegment(sketch, "E903", {"start": v(2.51, -2.8) * mm, "end": v(2.52, -2.83) * mm});
            skLineSegment(sketch, "E904", {"start": v(2.52, -2.83) * mm, "end": v(2.54, -3.06) * mm});
            skLineSegment(sketch, "E905", {"start": v(2.54, -3.06) * mm, "end": v(2.54, -3.08) * mm});
            skLineSegment(sketch, "E906", {"start": v(2.54, -3.08) * mm, "end": v(2.52, -3.1) * mm});
            skLineSegment(sketch, "E907", {"start": v(2.52, -3.1) * mm, "end": v(2.3, -3.19) * mm});
            skLineSegment(sketch, "E908", {"start": v(2.3, -3.19) * mm, "end": v(2.29, -3.2) * mm});
            skLineSegment(sketch, "E909", {"start": v(2.29, -3.2) * mm, "end": v(2.28, -3.2) * mm});
            skLineSegment(sketch, "E910", {"start": v(2.28, -3.2) * mm, "end": v(2.26, -3.22) * mm});
            skLineSegment(sketch, "E911", {"start": v(2.26, -3.22) * mm, "end": v(2.25, -3.26) * mm});
            skLineSegment(sketch, "E912", {"start": v(2.25, -3.26) * mm, "end": v(2.26, -3.3) * mm});
            skLineSegment(sketch, "E913", {"start": v(2.26, -3.3) * mm, "end": v(2.28, -3.33) * mm});
            skLineSegment(sketch, "E914", {"start": v(2.28, -3.33) * mm, "end": v(2.29, -3.33) * mm});
            skLineSegment(sketch, "E915", {"start": v(2.29, -3.33) * mm, "end": v(2.3, -3.34) * mm});
            skLineSegment(sketch, "E916", {"start": v(2.3, -3.34) * mm, "end": v(2.52, -3.44) * mm});
            skLineSegment(sketch, "E917", {"start": v(2.52, -3.44) * mm, "end": v(2.54, -3.45) * mm});
            skLineSegment(sketch, "E918", {"start": v(2.54, -3.45) * mm, "end": v(2.54, -3.47) * mm});
            skLineSegment(sketch, "E919", {"start": v(2.54, -3.47) * mm, "end": v(2.52, -3.7) * mm});
            skLineSegment(sketch, "E920", {"start": v(2.52, -3.7) * mm, "end": v(2.51, -3.72) * mm});
            skLineSegment(sketch, "E921", {"start": v(2.51, -3.72) * mm, "end": v(2.51, -3.73) * mm});
            skLineSegment(sketch, "E922", {"start": v(2.51, -3.73) * mm, "end": v(2.51, -3.74) * mm});
            skLineSegment(sketch, "E923", {"start": v(2.51, -3.74) * mm, "end": v(2.52, -3.76) * mm});
            skLineSegment(sketch, "E924", {"start": v(2.52, -3.76) * mm, "end": v(2.54, -3.78) * mm});
            skLineSegment(sketch, "E925", {"start": v(2.54, -3.78) * mm, "end": v(2.55, -3.8) * mm});
            skLineSegment(sketch, "E926", {"start": v(2.55, -3.8) * mm, "end": v(2.57, -3.8) * mm});
            skLineSegment(sketch, "E927", {"start": v(2.57, -3.8) * mm, "end": v(2.6, -3.8) * mm});
            skLineSegment(sketch, "E928", {"start": v(2.6, -3.8) * mm, "end": v(2.61, -3.8) * mm});
            skLineSegment(sketch, "E929", {"start": v(2.61, -3.8) * mm, "end": v(2.63, -3.8) * mm});
            skLineSegment(sketch, "E930", {"start": v(2.63, -3.8) * mm, "end": v(2.63, -3.8) * mm});
            skLineSegment(sketch, "E931", {"start": v(2.63, -3.8) * mm, "end": v(2.65, -3.78) * mm});
            skLineSegment(sketch, "E932", {"start": v(2.65, -3.78) * mm, "end": v(2.84, -3.64) * mm});
            skLineSegment(sketch, "E933", {"start": v(2.84, -3.64) * mm, "end": v(2.86, -3.63) * mm});
            skLineSegment(sketch, "E934", {"start": v(2.86, -3.63) * mm, "end": v(2.88, -3.64) * mm});
            skLineSegment(sketch, "E935", {"start": v(2.88, -3.64) * mm, "end": v(3.06, -3.78) * mm});
            skLineSegment(sketch, "E936", {"start": v(3.06, -3.78) * mm, "end": v(3.08, -3.8) * mm});
            skLineSegment(sketch, "E937", {"start": v(3.08, -3.8) * mm, "end": v(3.09, -3.8) * mm});
            skLineSegment(sketch, "E938", {"start": v(3.09, -3.8) * mm, "end": v(3.1, -3.8) * mm});
            skLineSegment(sketch, "E939", {"start": v(3.1, -3.8) * mm, "end": v(3.12, -3.8) * mm});
            skLineSegment(sketch, "E940", {"start": v(3.12, -3.8) * mm, "end": v(3.14, -3.8) * mm});
            skLineSegment(sketch, "E941", {"start": v(3.14, -3.8) * mm, "end": v(3.16, -3.8) * mm});
            skLineSegment(sketch, "E942", {"start": v(3.16, -3.8) * mm, "end": v(3.18, -3.78) * mm});
            skLineSegment(sketch, "E943", {"start": v(3.18, -3.78) * mm, "end": v(3.2, -3.76) * mm});
            skLineSegment(sketch, "E944", {"start": v(3.2, -3.76) * mm, "end": v(3.2, -3.74) * mm});
            skLineSegment(sketch, "E945", {"start": v(3.2, -3.74) * mm, "end": v(3.2, -3.73) * mm});
            skLineSegment(sketch, "E946", {"start": v(3.2, -3.73) * mm, "end": v(3.2, -3.72) * mm});
            skLineSegment(sketch, "E947", {"start": v(3.2, -3.72) * mm, "end": v(3.2, -3.7) * mm});
            skLineSegment(sketch, "E948", {"start": v(3.2, -3.7) * mm, "end": v(3.17, -3.47) * mm});
            skLineSegment(sketch, "E949", {"start": v(3.17, -3.47) * mm, "end": v(3.17, -3.45) * mm});
            skLineSegment(sketch, "E950", {"start": v(3.17, -3.45) * mm, "end": v(3.2, -3.44) * mm});
            skLineSegment(sketch, "E951", {"start": v(3.2, -3.44) * mm, "end": v(3.4, -3.34) * mm});
            skLineSegment(sketch, "E952", {"start": v(3.4, -3.34) * mm, "end": v(3.43, -3.33) * mm});
            skLineSegment(sketch, "E953", {"start": v(3.43, -3.33) * mm, "end": v(3.44, -3.33) * mm});
            skLineSegment(sketch, "E954", {"start": v(3.44, -3.33) * mm, "end": v(3.46, -3.3) * mm});
            skLineSegment(sketch, "E955", {"start": v(3.46, -3.3) * mm, "end": v(3.47, -3.26) * mm});
            skLineSegment(sketch, "E956", {"start": v(3.47, -3.26) * mm, "end": v(3.46, -3.22) * mm});
            skLineSegment(sketch, "E957", {"start": v(3.46, -3.22) * mm, "end": v(3.44, -3.2) * mm});
            skLineSegment(sketch, "E958", {"start": v(3.44, -3.2) * mm, "end": v(3.43, -3.2) * mm});
            skLineSegment(sketch, "E959", {"start": v(2.86, 1.96) * mm, "end": v(2.85, 1.96) * mm});
            skLineSegment(sketch, "E960", {"start": v(2.85, 1.96) * mm, "end": v(2.82, 1.97) * mm});
            skLineSegment(sketch, "E961", {"start": v(2.82, 1.97) * mm, "end": v(2.78, 1.98) * mm});
            skLineSegment(sketch, "E962", {"start": v(2.78, 1.98) * mm, "end": v(2.75, 2) * mm});
            skLineSegment(sketch, "E963", {"start": v(2.75, 2) * mm, "end": v(2.72, 2.02) * mm});
            skLineSegment(sketch, "E964", {"start": v(2.72, 2.02) * mm, "end": v(2.7, 2.05) * mm});
            skLineSegment(sketch, "E965", {"start": v(2.7, 2.05) * mm, "end": v(2.68, 2.08) * mm});
            skLineSegment(sketch, "E966", {"start": v(2.68, 2.08) * mm, "end": v(2.67, 2.12) * mm});
            skLineSegment(sketch, "E967", {"start": v(2.67, 2.12) * mm, "end": v(2.67, 2.14) * mm});
            skLineSegment(sketch, "E968", {"start": v(2.67, 2.14) * mm, "end": v(2.67, 2.15) * mm});
            skLineSegment(sketch, "E969", {"start": v(2.67, 2.15) * mm, "end": v(2.67, 2.16) * mm});
            skLineSegment(sketch, "E970", {"start": v(2.67, 2.16) * mm, "end": v(2.67, 2.2) * mm});
            skLineSegment(sketch, "E971", {"start": v(2.67, 2.2) * mm, "end": v(2.68, 2.23) * mm});
            skLineSegment(sketch, "E972", {"start": v(2.68, 2.23) * mm, "end": v(2.7, 2.26) * mm});
            skLineSegment(sketch, "E973", {"start": v(2.7, 2.26) * mm, "end": v(2.72, 2.29) * mm});
            skLineSegment(sketch, "E974", {"start": v(2.72, 2.29) * mm, "end": v(2.75, 2.3) * mm});
            skLineSegment(sketch, "E975", {"start": v(2.75, 2.3) * mm, "end": v(2.78, 2.33) * mm});
            skLineSegment(sketch, "E976", {"start": v(2.78, 2.33) * mm, "end": v(2.82, 2.34) * mm});
            skLineSegment(sketch, "E977", {"start": v(2.82, 2.34) * mm, "end": v(2.85, 2.34) * mm});
            skLineSegment(sketch, "E978", {"start": v(2.85, 2.34) * mm, "end": v(2.86, 2.34) * mm});
            skLineSegment(sketch, "E979", {"start": v(2.86, 2.34) * mm, "end": v(2.87, 2.34) * mm});
            skLineSegment(sketch, "E980", {"start": v(2.87, 2.34) * mm, "end": v(2.9, 2.34) * mm});
            skLineSegment(sketch, "E981", {"start": v(2.9, 2.34) * mm, "end": v(2.93, 2.33) * mm});
            skLineSegment(sketch, "E982", {"start": v(2.93, 2.33) * mm, "end": v(2.96, 2.3) * mm});
            skLineSegment(sketch, "E983", {"start": v(2.96, 2.3) * mm, "end": v(3, 2.29) * mm});
            skLineSegment(sketch, "E984", {"start": v(3, 2.29) * mm, "end": v(3.01, 2.26) * mm});
            skLineSegment(sketch, "E985", {"start": v(3.01, 2.26) * mm, "end": v(3.03, 2.23) * mm});
            skLineSegment(sketch, "E986", {"start": v(3.03, 2.23) * mm, "end": v(3.04, 2.2) * mm});
            skLineSegment(sketch, "E987", {"start": v(3.04, 2.2) * mm, "end": v(3.05, 2.16) * mm});
            skLineSegment(sketch, "E988", {"start": v(3.05, 2.16) * mm, "end": v(3.05, 2.15) * mm});
            skLineSegment(sketch, "E989", {"start": v(3.05, 2.15) * mm, "end": v(3.05, 2.14) * mm});
            skLineSegment(sketch, "E990", {"start": v(3.05, 2.14) * mm, "end": v(3.04, 2.12) * mm});
            skLineSegment(sketch, "E991", {"start": v(3.04, 2.12) * mm, "end": v(3.03, 2.08) * mm});
            skLineSegment(sketch, "E992", {"start": v(3.03, 2.08) * mm, "end": v(3.01, 2.05) * mm});
            skLineSegment(sketch, "E993", {"start": v(3.01, 2.05) * mm, "end": v(3, 2.02) * mm});
            skLineSegment(sketch, "E994", {"start": v(3, 2.02) * mm, "end": v(2.96, 2) * mm});
            skLineSegment(sketch, "E995", {"start": v(2.96, 2) * mm, "end": v(2.93, 1.98) * mm});
            skLineSegment(sketch, "E996", {"start": v(2.93, 1.98) * mm, "end": v(2.9, 1.97) * mm});
            skLineSegment(sketch, "E997", {"start": v(2.9, 1.97) * mm, "end": v(2.87, 1.96) * mm});
            skLineSegment(sketch, "E998", {"start": v(2.87, 1.96) * mm, "end": v(2.86, 1.96) * mm});
            skLineSegment(sketch, "E999", {"start": v(3.72, 1.74) * mm, "end": v(3.5, 1.86) * mm});
            skLineSegment(sketch, "E1000", {"start": v(3.5, 1.86) * mm, "end": v(3.69, 1.91) * mm});
            skLineSegment(sketch, "E1001", {"start": v(3.69, 1.91) * mm, "end": v(3.7, 1.91) * mm});
            skLineSegment(sketch, "E1002", {"start": v(3.7, 1.91) * mm, "end": v(3.71, 1.92) * mm});
            skLineSegment(sketch, "E1003", {"start": v(3.71, 1.92) * mm, "end": v(3.73, 1.95) * mm});
            skLineSegment(sketch, "E1004", {"start": v(3.73, 1.95) * mm, "end": v(3.74, 1.97) * mm});
            skLineSegment(sketch, "E1005", {"start": v(3.74, 1.97) * mm, "end": v(3.74, 2) * mm});
            skLineSegment(sketch, "E1006", {"start": v(3.74, 2) * mm, "end": v(3.74, 2) * mm});
            skLineSegment(sketch, "E1007", {"start": v(3.74, 2) * mm, "end": v(3.72, 2.03) * mm});
            skLineSegment(sketch, "E1008", {"start": v(3.72, 2.03) * mm, "end": v(3.7, 2.05) * mm});
            skLineSegment(sketch, "E1009", {"start": v(3.7, 2.05) * mm, "end": v(3.68, 2.05) * mm});
            skLineSegment(sketch, "E1010", {"start": v(3.68, 2.05) * mm, "end": v(3.66, 2.05) * mm});
            skLineSegment(sketch, "E1011", {"start": v(3.66, 2.05) * mm, "end": v(3.65, 2.05) * mm});
            skLineSegment(sketch, "E1012", {"start": v(3.65, 2.05) * mm, "end": v(3.33, 1.97) * mm});
            skLineSegment(sketch, "E1013", {"start": v(3.33, 1.97) * mm, "end": v(3.32, 1.97) * mm});
            skLineSegment(sketch, "E1014", {"start": v(3.32, 1.97) * mm, "end": v(3.3, 1.99) * mm});
            skLineSegment(sketch, "E1015", {"start": v(3.3, 1.99) * mm, "end": v(3.2, 2.14) * mm});
            skLineSegment(sketch, "E1016", {"start": v(3.2, 2.14) * mm, "end": v(3.18, 2.15) * mm});
            skLineSegment(sketch, "E1017", {"start": v(3.18, 2.15) * mm, "end": v(3.2, 2.17) * mm});
            skLineSegment(sketch, "E1018", {"start": v(3.2, 2.17) * mm, "end": v(3.3, 2.32) * mm});
            skLineSegment(sketch, "E1019", {"start": v(3.3, 2.32) * mm, "end": v(3.32, 2.34) * mm});
            skLineSegment(sketch, "E1020", {"start": v(3.32, 2.34) * mm, "end": v(3.33, 2.34) * mm});
            skLineSegment(sketch, "E1021", {"start": v(3.33, 2.34) * mm, "end": v(3.65, 2.25) * mm});
            skLineSegment(sketch, "E1022", {"start": v(3.65, 2.25) * mm, "end": v(3.66, 2.25) * mm});
            skLineSegment(sketch, "E1023", {"start": v(3.66, 2.25) * mm, "end": v(3.68, 2.25) * mm});
            skLineSegment(sketch, "E1024", {"start": v(3.68, 2.25) * mm, "end": v(3.7, 2.26) * mm});
            skLineSegment(sketch, "E1025", {"start": v(3.7, 2.26) * mm, "end": v(3.72, 2.28) * mm});
            skLineSegment(sketch, "E1026", {"start": v(3.72, 2.28) * mm, "end": v(3.74, 2.3) * mm});
            skLineSegment(sketch, "E1027", {"start": v(3.74, 2.3) * mm, "end": v(3.74, 2.3) * mm});
            skLineSegment(sketch, "E1028", {"start": v(3.74, 2.3) * mm, "end": v(3.74, 2.31) * mm});
            skLineSegment(sketch, "E1029", {"start": v(3.74, 2.31) * mm, "end": v(3.74, 2.33) * mm});
            skLineSegment(sketch, "E1030", {"start": v(3.74, 2.33) * mm, "end": v(3.73, 2.36) * mm});
            skLineSegment(sketch, "E1031", {"start": v(3.73, 2.36) * mm, "end": v(3.71, 2.38) * mm});
            skLineSegment(sketch, "E1032", {"start": v(3.71, 2.38) * mm, "end": v(3.7, 2.4) * mm});
            skLineSegment(sketch, "E1033", {"start": v(3.7, 2.4) * mm, "end": v(3.69, 2.4) * mm});
            skLineSegment(sketch, "E1034", {"start": v(3.69, 2.4) * mm, "end": v(3.5, 2.44) * mm});
            skLineSegment(sketch, "E1035", {"start": v(3.5, 2.44) * mm, "end": v(3.72, 2.57) * mm});
            skLineSegment(sketch, "E1036", {"start": v(3.72, 2.57) * mm, "end": v(3.73, 2.57) * mm});
            skLineSegment(sketch, "E1037", {"start": v(3.73, 2.57) * mm, "end": v(3.74, 2.59) * mm});
            skLineSegment(sketch, "E1038", {"start": v(3.74, 2.59) * mm, "end": v(3.76, 2.61) * mm});
            skLineSegment(sketch, "E1039", {"start": v(3.76, 2.61) * mm, "end": v(3.76, 2.64) * mm});
            skLineSegment(sketch, "E1040", {"start": v(3.76, 2.64) * mm, "end": v(3.75, 2.66) * mm});
            skLineSegment(sketch, "E1041", {"start": v(3.75, 2.66) * mm, "end": v(3.75, 2.67) * mm});
            skLineSegment(sketch, "E1042", {"start": v(3.75, 2.67) * mm, "end": v(3.75, 2.67) * mm});
            skLineSegment(sketch, "E1043", {"start": v(3.75, 2.67) * mm, "end": v(3.73, 2.7) * mm});
            skLineSegment(sketch, "E1044", {"start": v(3.73, 2.7) * mm, "end": v(3.7, 2.7) * mm});
            skLineSegment(sketch, "E1045", {"start": v(3.7, 2.7) * mm, "end": v(3.68, 2.7) * mm});
            skLineSegment(sketch, "E1046", {"start": v(3.68, 2.7) * mm, "end": v(3.66, 2.7) * mm});
            skLineSegment(sketch, "E1047", {"start": v(3.66, 2.7) * mm, "end": v(3.65, 2.7) * mm});
            skLineSegment(sketch, "E1048", {"start": v(3.65, 2.7) * mm, "end": v(3.43, 2.57) * mm});
            skLineSegment(sketch, "E1049", {"start": v(3.43, 2.57) * mm, "end": v(3.48, 2.75) * mm});
            skLineSegment(sketch, "E1050", {"start": v(3.48, 2.75) * mm, "end": v(3.48, 2.76) * mm});
            skLineSegment(sketch, "E1051", {"start": v(3.48, 2.76) * mm, "end": v(3.48, 2.78) * mm});
            skLineSegment(sketch, "E1052", {"start": v(3.48, 2.78) * mm, "end": v(3.47, 2.8) * mm});
            skLineSegment(sketch, "E1053", {"start": v(3.47, 2.8) * mm, "end": v(3.45, 2.83) * mm});
            skLineSegment(sketch, "E1054", {"start": v(3.45, 2.83) * mm, "end": v(3.44, 2.84) * mm});
            skLineSegment(sketch, "E1055", {"start": v(3.44, 2.84) * mm, "end": v(3.43, 2.84) * mm});
            skLineSegment(sketch, "E1056", {"start": v(3.43, 2.84) * mm, "end": v(3.42, 2.84) * mm});
            skLineSegment(sketch, "E1057", {"start": v(3.42, 2.84) * mm, "end": v(3.4, 2.84) * mm});
            skLineSegment(sketch, "E1058", {"start": v(3.4, 2.84) * mm, "end": v(3.37, 2.83) * mm});
            skLineSegment(sketch, "E1059", {"start": v(3.37, 2.83) * mm, "end": v(3.35, 2.81) * mm});
            skLineSegment(sketch, "E1060", {"start": v(3.35, 2.81) * mm, "end": v(3.34, 2.8) * mm});
            skLineSegment(sketch, "E1061", {"start": v(3.34, 2.8) * mm, "end": v(3.34, 2.79) * mm});
            skLineSegment(sketch, "E1062", {"start": v(3.34, 2.79) * mm, "end": v(3.25, 2.47) * mm});
            skLineSegment(sketch, "E1063", {"start": v(3.25, 2.47) * mm, "end": v(3.25, 2.46) * mm});
            skLineSegment(sketch, "E1064", {"start": v(3.25, 2.46) * mm, "end": v(3.23, 2.46) * mm});
            skLineSegment(sketch, "E1065", {"start": v(3.23, 2.46) * mm, "end": v(3.04, 2.44) * mm});
            skLineSegment(sketch, "E1066", {"start": v(3.04, 2.44) * mm, "end": v(3.02, 2.44) * mm});
            skLineSegment(sketch, "E1067", {"start": v(3.02, 2.44) * mm, "end": v(3.01, 2.45) * mm});
            skLineSegment(sketch, "E1068", {"start": v(3.01, 2.45) * mm, "end": v(2.94, 2.63) * mm});
            skLineSegment(sketch, "E1069", {"start": v(2.94, 2.63) * mm, "end": v(2.93, 2.64) * mm});
            skLineSegment(sketch, "E1070", {"start": v(2.93, 2.64) * mm, "end": v(2.93, 2.65) * mm});
            skLineSegment(sketch, "E1071", {"start": v(2.93, 2.65) * mm, "end": v(3.17, 2.89) * mm});
            skLineSegment(sketch, "E1072", {"start": v(3.17, 2.89) * mm, "end": v(3.17, 2.9) * mm});
            skLineSegment(sketch, "E1073", {"start": v(3.17, 2.9) * mm, "end": v(3.18, 2.91) * mm});
            skLineSegment(sketch, "E1074", {"start": v(3.18, 2.91) * mm, "end": v(3.19, 2.94) * mm});
            skLineSegment(sketch, "E1075", {"start": v(3.19, 2.94) * mm, "end": v(3.18, 2.97) * mm});
            skLineSegment(sketch, "E1076", {"start": v(3.18, 2.97) * mm, "end": v(3.17, 2.99) * mm});
            skLineSegment(sketch, "E1077", {"start": v(3.17, 2.99) * mm, "end": v(3.17, 3) * mm});
            skLineSegment(sketch, "E1078", {"start": v(3.17, 3) * mm, "end": v(3.16, 3) * mm});
            skLineSegment(sketch, "E1079", {"start": v(3.16, 3) * mm, "end": v(3.14, 3) * mm});
            skLineSegment(sketch, "E1080", {"start": v(3.14, 3) * mm, "end": v(3.11, 3.01) * mm});
            skLineSegment(sketch, "E1081", {"start": v(3.11, 3.01) * mm, "end": v(3.09, 3) * mm});
            skLineSegment(sketch, "E1082", {"start": v(3.09, 3) * mm, "end": v(3.07, 3) * mm});
            skLineSegment(sketch, "E1083", {"start": v(3.07, 3) * mm, "end": v(3.06, 3) * mm});
            skLineSegment(sketch, "E1084", {"start": v(3.06, 3) * mm, "end": v(2.93, 2.86) * mm});
            skLineSegment(sketch, "E1085", {"start": v(2.93, 2.86) * mm, "end": v(2.93, 3.11) * mm});
            skLineSegment(sketch, "E1086", {"start": v(2.93, 3.11) * mm, "end": v(2.93, 3.12) * mm});
            skLineSegment(sketch, "E1087", {"start": v(2.93, 3.12) * mm, "end": v(2.92, 3.14) * mm});
            skLineSegment(sketch, "E1088", {"start": v(2.92, 3.14) * mm, "end": v(2.9, 3.16) * mm});
            skLineSegment(sketch, "E1089", {"start": v(2.9, 3.16) * mm, "end": v(2.89, 3.18) * mm});
            skLineSegment(sketch, "E1090", {"start": v(2.89, 3.18) * mm, "end": v(2.86, 3.18) * mm});
            skLineSegment(sketch, "E1091", {"start": v(2.86, 3.18) * mm, "end": v(2.86, 3.18) * mm});
            skLineSegment(sketch, "E1092", {"start": v(2.86, 3.18) * mm, "end": v(2.85, 3.18) * mm});
            skLineSegment(sketch, "E1093", {"start": v(2.85, 3.18) * mm, "end": v(2.83, 3.18) * mm});
            skLineSegment(sketch, "E1094", {"start": v(2.83, 3.18) * mm, "end": v(2.8, 3.16) * mm});
            skLineSegment(sketch, "E1095", {"start": v(2.8, 3.16) * mm, "end": v(2.79, 3.14) * mm});
            skLineSegment(sketch, "E1096", {"start": v(2.79, 3.14) * mm, "end": v(2.78, 3.12) * mm});
            skLineSegment(sketch, "E1097", {"start": v(2.78, 3.12) * mm, "end": v(2.78, 3.11) * mm});
            skLineSegment(sketch, "E1098", {"start": v(2.78, 3.11) * mm, "end": v(2.78, 2.86) * mm});
            skLineSegment(sketch, "E1099", {"start": v(2.78, 2.86) * mm, "end": v(2.65, 3) * mm});
            skLineSegment(sketch, "E1100", {"start": v(2.65, 3) * mm, "end": v(2.65, 3) * mm});
            skLineSegment(sketch, "E1101", {"start": v(2.65, 3) * mm, "end": v(2.63, 3) * mm});
            skLineSegment(sketch, "E1102", {"start": v(2.63, 3) * mm, "end": v(2.6, 3.01) * mm});
            skLineSegment(sketch, "E1103", {"start": v(2.6, 3.01) * mm, "end": v(2.57, 3) * mm});
            skLineSegment(sketch, "E1104", {"start": v(2.57, 3) * mm, "end": v(2.55, 3) * mm});
            skLineSegment(sketch, "E1105", {"start": v(2.55, 3) * mm, "end": v(2.55, 3) * mm});
            skLineSegment(sketch, "E1106", {"start": v(2.55, 3) * mm, "end": v(2.54, 2.99) * mm});
            skLineSegment(sketch, "E1107", {"start": v(2.54, 2.99) * mm, "end": v(2.53, 2.97) * mm});
            skLineSegment(sketch, "E1108", {"start": v(2.53, 2.97) * mm, "end": v(2.53, 2.94) * mm});
            skLineSegment(sketch, "E1109", {"start": v(2.53, 2.94) * mm, "end": v(2.53, 2.91) * mm});
            skLineSegment(sketch, "E1110", {"start": v(2.53, 2.91) * mm, "end": v(2.54, 2.9) * mm});
            skLineSegment(sketch, "E1111", {"start": v(2.54, 2.9) * mm, "end": v(2.55, 2.89) * mm});
            skLineSegment(sketch, "E1112", {"start": v(2.55, 2.89) * mm, "end": v(2.78, 2.65) * mm});
            skLineSegment(sketch, "E1113", {"start": v(2.78, 2.65) * mm, "end": v(2.78, 2.64) * mm});
            skLineSegment(sketch, "E1114", {"start": v(2.78, 2.64) * mm, "end": v(2.78, 2.63) * mm});
            skLineSegment(sketch, "E1115", {"start": v(2.78, 2.63) * mm, "end": v(2.7, 2.45) * mm});
            skLineSegment(sketch, "E1116", {"start": v(2.7, 2.45) * mm, "end": v(2.7, 2.44) * mm});
            skLineSegment(sketch, "E1117", {"start": v(2.7, 2.44) * mm, "end": v(2.67, 2.44) * mm});
            skLineSegment(sketch, "E1118", {"start": v(2.67, 2.44) * mm, "end": v(2.49, 2.46) * mm});
            skLineSegment(sketch, "E1119", {"start": v(2.49, 2.46) * mm, "end": v(2.47, 2.46) * mm});
            skLineSegment(sketch, "E1120", {"start": v(2.47, 2.46) * mm, "end": v(2.46, 2.47) * mm});
            skLineSegment(sketch, "E1121", {"start": v(2.46, 2.47) * mm, "end": v(2.37, 2.79) * mm});
            skLineSegment(sketch, "E1122", {"start": v(2.37, 2.79) * mm, "end": v(2.37, 2.8) * mm});
            skLineSegment(sketch, "E1123", {"start": v(2.37, 2.8) * mm, "end": v(2.36, 2.81) * mm});
            skLineSegment(sketch, "E1124", {"start": v(2.36, 2.81) * mm, "end": v(2.34, 2.83) * mm});
            skLineSegment(sketch, "E1125", {"start": v(2.34, 2.83) * mm, "end": v(2.31, 2.84) * mm});
            skLineSegment(sketch, "E1126", {"start": v(2.31, 2.84) * mm, "end": v(2.3, 2.84) * mm});
            skLineSegment(sketch, "E1127", {"start": v(2.3, 2.84) * mm, "end": v(2.29, 2.84) * mm});
            skLineSegment(sketch, "E1128", {"start": v(2.29, 2.84) * mm, "end": v(2.28, 2.84) * mm});
            skLineSegment(sketch, "E1129", {"start": v(2.28, 2.84) * mm, "end": v(2.26, 2.83) * mm});
            skLineSegment(sketch, "E1130", {"start": v(2.26, 2.83) * mm, "end": v(2.24, 2.8) * mm});
            skLineSegment(sketch, "E1131", {"start": v(2.24, 2.8) * mm, "end": v(2.23, 2.78) * mm});
            skLineSegment(sketch, "E1132", {"start": v(2.23, 2.78) * mm, "end": v(2.23, 2.76) * mm});
            skLineSegment(sketch, "E1133", {"start": v(2.23, 2.76) * mm, "end": v(2.23, 2.75) * mm});
            skLineSegment(sketch, "E1134", {"start": v(2.23, 2.75) * mm, "end": v(2.28, 2.57) * mm});
            skLineSegment(sketch, "E1135", {"start": v(2.28, 2.57) * mm, "end": v(2.06, 2.7) * mm});
            skLineSegment(sketch, "E1136", {"start": v(2.06, 2.7) * mm, "end": v(2.06, 2.7) * mm});
            skLineSegment(sketch, "E1137", {"start": v(2.06, 2.7) * mm, "end": v(2.04, 2.7) * mm});
            skLineSegment(sketch, "E1138", {"start": v(2.04, 2.7) * mm, "end": v(2, 2.7) * mm});
            skLineSegment(sketch, "E1139", {"start": v(2, 2.7) * mm, "end": v(1.98, 2.7) * mm});
            skLineSegment(sketch, "E1140", {"start": v(1.98, 2.7) * mm, "end": v(1.97, 2.67) * mm});
            skLineSegment(sketch, "E1141", {"start": v(1.97, 2.67) * mm, "end": v(1.96, 2.67) * mm});
            skLineSegment(sketch, "E1142", {"start": v(1.96, 2.67) * mm, "end": v(1.96, 2.66) * mm});
            skLineSegment(sketch, "E1143", {"start": v(1.96, 2.66) * mm, "end": v(1.95, 2.64) * mm});
            skLineSegment(sketch, "E1144", {"start": v(1.95, 2.64) * mm, "end": v(1.96, 2.61) * mm});
            skLineSegment(sketch, "E1145", {"start": v(1.96, 2.61) * mm, "end": v(1.97, 2.59) * mm});
            skLineSegment(sketch, "E1146", {"start": v(1.97, 2.59) * mm, "end": v(1.98, 2.57) * mm});
            skLineSegment(sketch, "E1147", {"start": v(1.98, 2.57) * mm, "end": v(2, 2.57) * mm});
            skLineSegment(sketch, "E1148", {"start": v(2, 2.57) * mm, "end": v(2.2, 2.44) * mm});
            skLineSegment(sketch, "E1149", {"start": v(2.2, 2.44) * mm, "end": v(2.03, 2.4) * mm});
            skLineSegment(sketch, "E1150", {"start": v(2.03, 2.4) * mm, "end": v(2.02, 2.4) * mm});
            skLineSegment(sketch, "E1151", {"start": v(2.02, 2.4) * mm, "end": v(2, 2.38) * mm});
            skLineSegment(sketch, "E1152", {"start": v(2, 2.38) * mm, "end": v(1.98, 2.36) * mm});
            skLineSegment(sketch, "E1153", {"start": v(1.98, 2.36) * mm, "end": v(1.97, 2.33) * mm});
            skLineSegment(sketch, "E1154", {"start": v(1.97, 2.33) * mm, "end": v(1.97, 2.31) * mm});
            skLineSegment(sketch, "E1155", {"start": v(1.97, 2.31) * mm, "end": v(1.98, 2.3) * mm});
            skLineSegment(sketch, "E1156", {"start": v(1.98, 2.3) * mm, "end": v(1.98, 2.3) * mm});
            skLineSegment(sketch, "E1157", {"start": v(1.98, 2.3) * mm, "end": v(1.99, 2.28) * mm});
            skLineSegment(sketch, "E1158", {"start": v(1.99, 2.28) * mm, "end": v(2.01, 2.26) * mm});
            skLineSegment(sketch, "E1159", {"start": v(2.01, 2.26) * mm, "end": v(2.04, 2.25) * mm});
            skLineSegment(sketch, "E1160", {"start": v(2.04, 2.25) * mm, "end": v(2.06, 2.25) * mm});
            skLineSegment(sketch, "E1161", {"start": v(2.06, 2.25) * mm, "end": v(2.07, 2.25) * mm});
            skLineSegment(sketch, "E1162", {"start": v(2.07, 2.25) * mm, "end": v(2.39, 2.34) * mm});
            skLineSegment(sketch, "E1163", {"start": v(2.39, 2.34) * mm, "end": v(2.4, 2.34) * mm});
            skLineSegment(sketch, "E1164", {"start": v(2.4, 2.34) * mm, "end": v(2.4, 2.32) * mm});
            skLineSegment(sketch, "E1165", {"start": v(2.4, 2.32) * mm, "end": v(2.52, 2.17) * mm});
            skLineSegment(sketch, "E1166", {"start": v(2.52, 2.17) * mm, "end": v(2.53, 2.15) * mm});
            skLineSegment(sketch, "E1167", {"start": v(2.53, 2.15) * mm, "end": v(2.52, 2.14) * mm});
            skLineSegment(sketch, "E1168", {"start": v(2.52, 2.14) * mm, "end": v(2.4, 1.99) * mm});
            skLineSegment(sketch, "E1169", {"start": v(2.4, 1.99) * mm, "end": v(2.4, 1.97) * mm});
            skLineSegment(sketch, "E1170", {"start": v(2.4, 1.97) * mm, "end": v(2.39, 1.97) * mm});
            skLineSegment(sketch, "E1171", {"start": v(2.39, 1.97) * mm, "end": v(2.07, 2.05) * mm});
            skLineSegment(sketch, "E1172", {"start": v(2.07, 2.05) * mm, "end": v(2.06, 2.05) * mm});
            skLineSegment(sketch, "E1173", {"start": v(2.06, 2.05) * mm, "end": v(2.04, 2.05) * mm});
            skLineSegment(sketch, "E1174", {"start": v(2.04, 2.05) * mm, "end": v(2.01, 2.05) * mm});
            skLineSegment(sketch, "E1175", {"start": v(2.01, 2.05) * mm, "end": v(1.99, 2.03) * mm});
            skLineSegment(sketch, "E1176", {"start": v(1.99, 2.03) * mm, "end": v(1.98, 2) * mm});
            skLineSegment(sketch, "E1177", {"start": v(1.98, 2) * mm, "end": v(1.98, 2) * mm});
            skLineSegment(sketch, "E1178", {"start": v(1.98, 2) * mm, "end": v(1.97, 2) * mm});
            skLineSegment(sketch, "E1179", {"start": v(1.97, 2) * mm, "end": v(1.97, 1.97) * mm});
            skLineSegment(sketch, "E1180", {"start": v(1.97, 1.97) * mm, "end": v(1.98, 1.95) * mm});
            skLineSegment(sketch, "E1181", {"start": v(1.98, 1.95) * mm, "end": v(2, 1.92) * mm});
            skLineSegment(sketch, "E1182", {"start": v(2, 1.92) * mm, "end": v(2.02, 1.91) * mm});
            skLineSegment(sketch, "E1183", {"start": v(2.02, 1.91) * mm, "end": v(2.03, 1.91) * mm});
            skLineSegment(sketch, "E1184", {"start": v(2.03, 1.91) * mm, "end": v(2.2, 1.86) * mm});
            skLineSegment(sketch, "E1185", {"start": v(2.2, 1.86) * mm, "end": v(2, 1.74) * mm});
            skLineSegment(sketch, "E1186", {"start": v(2, 1.74) * mm, "end": v(1.98, 1.73) * mm});
            skLineSegment(sketch, "E1187", {"start": v(1.98, 1.73) * mm, "end": v(1.97, 1.72) * mm});
            skLineSegment(sketch, "E1188", {"start": v(1.97, 1.72) * mm, "end": v(1.96, 1.7) * mm});
            skLineSegment(sketch, "E1189", {"start": v(1.96, 1.7) * mm, "end": v(1.95, 1.66) * mm});
            skLineSegment(sketch, "E1190", {"start": v(1.95, 1.66) * mm, "end": v(1.96, 1.64) * mm});
            skLineSegment(sketch, "E1191", {"start": v(1.96, 1.64) * mm, "end": v(1.96, 1.64) * mm});
            skLineSegment(sketch, "E1192", {"start": v(1.96, 1.64) * mm, "end": v(1.97, 1.63) * mm});
            skLineSegment(sketch, "E1193", {"start": v(1.97, 1.63) * mm, "end": v(1.98, 1.62) * mm});
            skLineSegment(sketch, "E1194", {"start": v(1.98, 1.62) * mm, "end": v(2, 1.6) * mm});
            skLineSegment(sketch, "E1195", {"start": v(2, 1.6) * mm, "end": v(2.04, 1.6) * mm});
            skLineSegment(sketch, "E1196", {"start": v(2.04, 1.6) * mm, "end": v(2.06, 1.6) * mm});
            skLineSegment(sketch, "E1197", {"start": v(2.06, 1.6) * mm, "end": v(2.06, 1.61) * mm});
            skLineSegment(sketch, "E1198", {"start": v(2.06, 1.61) * mm, "end": v(2.28, 1.74) * mm});
            skLineSegment(sketch, "E1199", {"start": v(2.28, 1.74) * mm, "end": v(2.23, 1.56) * mm});
            skLineSegment(sketch, "E1200", {"start": v(2.23, 1.56) * mm, "end": v(2.23, 1.55) * mm});
            skLineSegment(sketch, "E1201", {"start": v(2.23, 1.55) * mm, "end": v(2.23, 1.53) * mm});
            skLineSegment(sketch, "E1202", {"start": v(2.23, 1.53) * mm, "end": v(2.24, 1.5) * mm});
            skLineSegment(sketch, "E1203", {"start": v(2.24, 1.5) * mm, "end": v(2.26, 1.48) * mm});
            skLineSegment(sketch, "E1204", {"start": v(2.26, 1.48) * mm, "end": v(2.28, 1.47) * mm});
            skLineSegment(sketch, "E1205", {"start": v(2.28, 1.47) * mm, "end": v(2.29, 1.47) * mm});
            skLineSegment(sketch, "E1206", {"start": v(2.29, 1.47) * mm, "end": v(2.3, 1.46) * mm});
            skLineSegment(sketch, "E1207", {"start": v(2.3, 1.46) * mm, "end": v(2.31, 1.46) * mm});
            skLineSegment(sketch, "E1208", {"start": v(2.31, 1.46) * mm, "end": v(2.34, 1.47) * mm});
            skLineSegment(sketch, "E1209", {"start": v(2.34, 1.47) * mm, "end": v(2.36, 1.5) * mm});
            skLineSegment(sketch, "E1210", {"start": v(2.36, 1.5) * mm, "end": v(2.37, 1.51) * mm});
            skLineSegment(sketch, "E1211", {"start": v(2.37, 1.51) * mm, "end": v(2.37, 1.52) * mm});
            skLineSegment(sketch, "E1212", {"start": v(2.37, 1.52) * mm, "end": v(2.46, 1.84) * mm});
            skLineSegment(sketch, "E1213", {"start": v(2.46, 1.84) * mm, "end": v(2.47, 1.85) * mm});
            skLineSegment(sketch, "E1214", {"start": v(2.47, 1.85) * mm, "end": v(2.49, 1.85) * mm});
            skLineSegment(sketch, "E1215", {"start": v(2.49, 1.85) * mm, "end": v(2.67, 1.87) * mm});
            skLineSegment(sketch, "E1216", {"start": v(2.67, 1.87) * mm, "end": v(2.7, 1.87) * mm});
            skLineSegment(sketch, "E1217", {"start": v(2.7, 1.87) * mm, "end": v(2.7, 1.85) * mm});
            skLineSegment(sketch, "E1218", {"start": v(2.7, 1.85) * mm, "end": v(2.78, 1.68) * mm});
            skLineSegment(sketch, "E1219", {"start": v(2.78, 1.68) * mm, "end": v(2.78, 1.66) * mm});
            skLineSegment(sketch, "E1220", {"start": v(2.78, 1.66) * mm, "end": v(2.78, 1.65) * mm});
            skLineSegment(sketch, "E1221", {"start": v(2.78, 1.65) * mm, "end": v(2.55, 1.42) * mm});
            skLineSegment(sketch, "E1222", {"start": v(2.55, 1.42) * mm, "end": v(2.54, 1.41) * mm});
            skLineSegment(sketch, "E1223", {"start": v(2.54, 1.41) * mm, "end": v(2.53, 1.4) * mm});
            skLineSegment(sketch, "E1224", {"start": v(2.53, 1.4) * mm, "end": v(2.53, 1.37) * mm});
            skLineSegment(sketch, "E1225", {"start": v(2.53, 1.37) * mm, "end": v(2.53, 1.34) * mm});
            skLineSegment(sketch, "E1226", {"start": v(2.53, 1.34) * mm, "end": v(2.54, 1.32) * mm});
            skLineSegment(sketch, "E1227", {"start": v(2.54, 1.32) * mm, "end": v(2.55, 1.31) * mm});
            skLineSegment(sketch, "E1228", {"start": v(2.55, 1.31) * mm, "end": v(2.55, 1.3) * mm});
            skLineSegment(sketch, "E1229", {"start": v(2.55, 1.3) * mm, "end": v(2.57, 1.3) * mm});
            skLineSegment(sketch, "E1230", {"start": v(2.57, 1.3) * mm, "end": v(2.6, 1.3) * mm});
            skLineSegment(sketch, "E1231", {"start": v(2.6, 1.3) * mm, "end": v(2.63, 1.3) * mm});
            skLineSegment(sketch, "E1232", {"start": v(2.63, 1.3) * mm, "end": v(2.65, 1.3) * mm});
            skLineSegment(sketch, "E1233", {"start": v(2.65, 1.3) * mm, "end": v(2.65, 1.31) * mm});
            skLineSegment(sketch, "E1234", {"start": v(2.65, 1.31) * mm, "end": v(2.78, 1.45) * mm});
            skLineSegment(sketch, "E1235", {"start": v(2.78, 1.45) * mm, "end": v(2.78, 1.2) * mm});
            skLineSegment(sketch, "E1236", {"start": v(2.78, 1.2) * mm, "end": v(2.78, 1.19) * mm});
            skLineSegment(sketch, "E1237", {"start": v(2.78, 1.19) * mm, "end": v(2.79, 1.17) * mm});
            skLineSegment(sketch, "E1238", {"start": v(2.79, 1.17) * mm, "end": v(2.8, 1.14) * mm});
            skLineSegment(sketch, "E1239", {"start": v(2.8, 1.14) * mm, "end": v(2.83, 1.13) * mm});
            skLineSegment(sketch, "E1240", {"start": v(2.83, 1.13) * mm, "end": v(2.85, 1.12) * mm});
            skLineSegment(sketch, "E1241", {"start": v(2.85, 1.12) * mm, "end": v(2.86, 1.12) * mm});
            skLineSegment(sketch, "E1242", {"start": v(2.86, 1.12) * mm, "end": v(2.86, 1.12) * mm});
            skLineSegment(sketch, "E1243", {"start": v(2.86, 1.12) * mm, "end": v(2.89, 1.13) * mm});
            skLineSegment(sketch, "E1244", {"start": v(2.89, 1.13) * mm, "end": v(2.9, 1.14) * mm});
            skLineSegment(sketch, "E1245", {"start": v(2.9, 1.14) * mm, "end": v(2.92, 1.17) * mm});
            skLineSegment(sketch, "E1246", {"start": v(2.92, 1.17) * mm, "end": v(2.93, 1.19) * mm});
            skLineSegment(sketch, "E1247", {"start": v(2.93, 1.19) * mm, "end": v(2.93, 1.2) * mm});
            skLineSegment(sketch, "E1248", {"start": v(2.93, 1.2) * mm, "end": v(2.93, 1.45) * mm});
            skLineSegment(sketch, "E1249", {"start": v(2.93, 1.45) * mm, "end": v(3.06, 1.31) * mm});
            skLineSegment(sketch, "E1250", {"start": v(3.06, 1.31) * mm, "end": v(3.07, 1.3) * mm});
            skLineSegment(sketch, "E1251", {"start": v(3.07, 1.3) * mm, "end": v(3.09, 1.3) * mm});
            skLineSegment(sketch, "E1252", {"start": v(3.09, 1.3) * mm, "end": v(3.11, 1.3) * mm});
            skLineSegment(sketch, "E1253", {"start": v(3.11, 1.3) * mm, "end": v(3.14, 1.3) * mm});
            skLineSegment(sketch, "E1254", {"start": v(3.14, 1.3) * mm, "end": v(3.16, 1.3) * mm});
            skLineSegment(sketch, "E1255", {"start": v(3.16, 1.3) * mm, "end": v(3.17, 1.31) * mm});
            skLineSegment(sketch, "E1256", {"start": v(3.17, 1.31) * mm, "end": v(3.17, 1.32) * mm});
            skLineSegment(sketch, "E1257", {"start": v(3.17, 1.32) * mm, "end": v(3.18, 1.34) * mm});
            skLineSegment(sketch, "E1258", {"start": v(3.18, 1.34) * mm, "end": v(3.19, 1.37) * mm});
            skLineSegment(sketch, "E1259", {"start": v(3.19, 1.37) * mm, "end": v(3.18, 1.4) * mm});
            skLineSegment(sketch, "E1260", {"start": v(3.18, 1.4) * mm, "end": v(3.17, 1.41) * mm});
            skLineSegment(sketch, "E1261", {"start": v(3.17, 1.41) * mm, "end": v(3.17, 1.42) * mm});
            skLineSegment(sketch, "E1262", {"start": v(3.17, 1.42) * mm, "end": v(2.93, 1.65) * mm});
            skLineSegment(sketch, "E1263", {"start": v(2.93, 1.65) * mm, "end": v(2.93, 1.66) * mm});
            skLineSegment(sketch, "E1264", {"start": v(2.93, 1.66) * mm, "end": v(2.94, 1.68) * mm});
            skLineSegment(sketch, "E1265", {"start": v(2.94, 1.68) * mm, "end": v(3.01, 1.85) * mm});
            skLineSegment(sketch, "E1266", {"start": v(3.01, 1.85) * mm, "end": v(3.02, 1.87) * mm});
            skLineSegment(sketch, "E1267", {"start": v(3.02, 1.87) * mm, "end": v(3.04, 1.87) * mm});
            skLineSegment(sketch, "E1268", {"start": v(3.04, 1.87) * mm, "end": v(3.23, 1.85) * mm});
            skLineSegment(sketch, "E1269", {"start": v(3.23, 1.85) * mm, "end": v(3.25, 1.85) * mm});
            skLineSegment(sketch, "E1270", {"start": v(3.25, 1.85) * mm, "end": v(3.25, 1.84) * mm});
            skLineSegment(sketch, "E1271", {"start": v(3.25, 1.84) * mm, "end": v(3.34, 1.52) * mm});
            skLineSegment(sketch, "E1272", {"start": v(3.34, 1.52) * mm, "end": v(3.34, 1.51) * mm});
            skLineSegment(sketch, "E1273", {"start": v(3.34, 1.51) * mm, "end": v(3.35, 1.5) * mm});
            skLineSegment(sketch, "E1274", {"start": v(3.35, 1.5) * mm, "end": v(3.37, 1.47) * mm});
            skLineSegment(sketch, "E1275", {"start": v(3.37, 1.47) * mm, "end": v(3.4, 1.46) * mm});
            skLineSegment(sketch, "E1276", {"start": v(3.4, 1.46) * mm, "end": v(3.42, 1.46) * mm});
            skLineSegment(sketch, "E1277", {"start": v(3.42, 1.46) * mm, "end": v(3.43, 1.47) * mm});
            skLineSegment(sketch, "E1278", {"start": v(3.43, 1.47) * mm, "end": v(3.44, 1.47) * mm});
            skLineSegment(sketch, "E1279", {"start": v(3.44, 1.47) * mm, "end": v(3.45, 1.48) * mm});
            skLineSegment(sketch, "E1280", {"start": v(3.45, 1.48) * mm, "end": v(3.47, 1.5) * mm});
            skLineSegment(sketch, "E1281", {"start": v(3.47, 1.5) * mm, "end": v(3.48, 1.53) * mm});
            skLineSegment(sketch, "E1282", {"start": v(3.48, 1.53) * mm, "end": v(3.48, 1.55) * mm});
            skLineSegment(sketch, "E1283", {"start": v(3.48, 1.55) * mm, "end": v(3.48, 1.56) * mm});
            skLineSegment(sketch, "E1284", {"start": v(3.48, 1.56) * mm, "end": v(3.43, 1.74) * mm});
            skLineSegment(sketch, "E1285", {"start": v(3.43, 1.74) * mm, "end": v(3.65, 1.61) * mm});
            skLineSegment(sketch, "E1286", {"start": v(3.65, 1.61) * mm, "end": v(3.66, 1.6) * mm});
            skLineSegment(sketch, "E1287", {"start": v(3.66, 1.6) * mm, "end": v(3.68, 1.6) * mm});
            skLineSegment(sketch, "E1288", {"start": v(3.68, 1.6) * mm, "end": v(3.7, 1.6) * mm});
            skLineSegment(sketch, "E1289", {"start": v(3.7, 1.6) * mm, "end": v(3.73, 1.62) * mm});
            skLineSegment(sketch, "E1290", {"start": v(3.73, 1.62) * mm, "end": v(3.75, 1.63) * mm});
            skLineSegment(sketch, "E1291", {"start": v(3.75, 1.63) * mm, "end": v(3.75, 1.64) * mm});
            skLineSegment(sketch, "E1292", {"start": v(3.75, 1.64) * mm, "end": v(3.75, 1.64) * mm});
            skLineSegment(sketch, "E1293", {"start": v(3.75, 1.64) * mm, "end": v(3.76, 1.66) * mm});
            skLineSegment(sketch, "E1294", {"start": v(3.76, 1.66) * mm, "end": v(3.76, 1.7) * mm});
            skLineSegment(sketch, "E1295", {"start": v(3.76, 1.7) * mm, "end": v(3.74, 1.72) * mm});
            skLineSegment(sketch, "E1296", {"start": v(3.74, 1.72) * mm, "end": v(3.73, 1.73) * mm});
            skLineSegment(sketch, "E1297", {"start": v(3.73, 1.73) * mm, "end": v(3.72, 1.74) * mm});
            skSolve(sketch);
        }
        {
            var Q0;
            {var subQ5=sQuery(id+"F0.wireOp",EDGE,"E155");Q0=makeQuery(id+"F0.imprint","IMPRINT",FACE,{"disambiguationData":[TD([[makeQuery(id+"F0.imprint","IMPRINT",EDGE,{"derivedFrom":subQ5}),-1.0]])]});}
            var Q1;
            {var subQ5=sQuery(id+"F0.wireOp",EDGE,"E142");Q1=makeQuery(id+"F0.imprint","IMPRINT",FACE,{"disambiguationData":[TD([[makeQuery(id+"F0.imprint","IMPRINT",EDGE,{"derivedFrom":subQ5}),-1.0]])]});}
            var Q2;
            {var subQ8=sQuery(id+"F0.wireOp",EDGE,"E14");Q2=makeQuery(id+"F0.imprint","IMPRINT",FACE,{"disambiguationData":[TD([[makeQuery(id+"F0.imprint","IMPRINT",EDGE,{"derivedFrom":subQ8}),1.0]])]});}
            var Q3;
            Q3=makeQuery(id+"F0.imprint","IMPRINT",FACE,{"disambiguationData":[TD([[makeQuery(id+"F0.imprint","IMPRINT",EDGE,{"derivedFrom":sQuery(id+"F0.wireOp",EDGE,"E134")}),-1.0]])]});
            var Q4;
            {var subQ5=sQuery(id+"F0.wireOp",EDGE,"E155");Q4=makeQuery(id+"F0.imprint","IMPRINT",FACE,{"disambiguationData":[TD([[makeQuery(id+"F0.imprint","IMPRINT",EDGE,{"derivedFrom":subQ5}),1.0]])]});}
            var Q5;
            {var subQ0=sQuery(id+"F0.wireOp",EDGE,"E119");Q5=makeQuery(id+"F0.imprint","IMPRINT",FACE,{"disambiguationData":[TD([[makeQuery(id+"F0.imprint","IMPRINT",EDGE,{"derivedFrom":subQ0}),-1.0]])]});}
            var Q6;
            {var subQ5=sQuery(id+"F0.wireOp",EDGE,"E106");Q6=makeQuery(id+"F0.imprint","IMPRINT",FACE,{"disambiguationData":[TD([[makeQuery(id+"F0.imprint","IMPRINT",EDGE,{"derivedFrom":subQ5}),-1.0]])]});}
            var Q7;
            Q7=makeQuery(id+"F0.imprint","IMPRINT",FACE,{"disambiguationData":[TD([[makeQuery(id+"F0.imprint","IMPRINT",EDGE,{"derivedFrom":sQuery(id+"F0.wireOp",EDGE,"E98")}),-1.0]])]});
            var Q8;
            {var subQ5=sQuery(id+"F0.wireOp",EDGE,"E276");Q8=makeQuery(id+"F0.imprint","IMPRINT",FACE,{"disambiguationData":[TD([[makeQuery(id+"F0.imprint","IMPRINT",EDGE,{"derivedFrom":subQ5}),-1.0]])]});}
            var Q9;
            {var subQ0=sQuery(id+"F0.wireOp",EDGE,"E289");Q9=makeQuery(id+"F0.imprint","IMPRINT",FACE,{"disambiguationData":[TD([[makeQuery(id+"F0.imprint","IMPRINT",EDGE,{"derivedFrom":subQ0}),-1.0]])]});}
            var Q10;
            Q10=makeQuery(id+"F0.imprint","IMPRINT",FACE,{"disambiguationData":[TD([[makeQuery(id+"F0.imprint","IMPRINT",EDGE,{"derivedFrom":sQuery(id+"F0.wireOp",EDGE,"E268")}),-1.0]])]});
            var Q11;
            {var subQ5=sQuery(id+"F0.wireOp",EDGE,"E325");Q11=makeQuery(id+"F0.imprint","IMPRINT",FACE,{"disambiguationData":[TD([[makeQuery(id+"F0.imprint","IMPRINT",EDGE,{"derivedFrom":subQ5}),1.0]])]});}
            var Q12;
            {var subQ5=sQuery(id+"F0.wireOp",EDGE,"E325");Q12=makeQuery(id+"F0.imprint","IMPRINT",FACE,{"disambiguationData":[TD([[makeQuery(id+"F0.imprint","IMPRINT",EDGE,{"derivedFrom":subQ5}),-1.0]])]});}
            var Q13;
            Q13=makeQuery(id+"F0.imprint","IMPRINT",FACE,{"disambiguationData":[TD([[makeQuery(id+"F0.imprint","IMPRINT",EDGE,{"derivedFrom":sQuery(id+"F0.wireOp",EDGE,"E304")}),-1.0]])]});
            var Q14;
            {var subQ5=sQuery(id+"F0.wireOp",EDGE,"E312");Q14=makeQuery(id+"F0.imprint","IMPRINT",FACE,{"disambiguationData":[TD([[makeQuery(id+"F0.imprint","IMPRINT",EDGE,{"derivedFrom":subQ5}),-1.0]])]});}
            var Q15;
            {var subQ8=sQuery(id+"F0.wireOp",EDGE,"E184");Q15=makeQuery(id+"F0.imprint","IMPRINT",FACE,{"disambiguationData":[TD([[makeQuery(id+"F0.imprint","IMPRINT",EDGE,{"derivedFrom":subQ8}),1.0]])]});}
            var Q16;
            {var subQ9=sQuery(id+"F0.wireOp",EDGE,"E289");Q16=makeQuery(id+"F0.imprint","IMPRINT",FACE,{"disambiguationData":[TD([[makeQuery(id+"F0.imprint","IMPRINT",EDGE,{"derivedFrom":subQ9}),1.0]])]});}
            var Q17;
            {var subQ0=sQuery(id+"F0.wireOp",EDGE,"E374");Q17=makeQuery(id+"F0.imprint","IMPRINT",FACE,{"disambiguationData":[TD([[makeQuery(id+"F0.imprint","IMPRINT",EDGE,{"derivedFrom":subQ0}),1.0]])]});}
            var Q18;
            {var subQ5=sQuery(id+"F0.wireOp",EDGE,"E409");Q18=makeQuery(id+"F0.imprint","IMPRINT",FACE,{"disambiguationData":[TD([[makeQuery(id+"F0.imprint","IMPRINT",EDGE,{"derivedFrom":subQ5}),1.0]])]});}
            var Q19;
            {var subQ0=sQuery(id+"F0.wireOp",EDGE,"E341");Q19=makeQuery(id+"F0.imprint","IMPRINT",FACE,{"disambiguationData":[TD([[makeQuery(id+"F0.imprint","IMPRINT",EDGE,{"derivedFrom":subQ0}),1.0]])]});}
            var Q20;
            {var subQ5=sQuery(id+"F0.wireOp",EDGE,"E422");Q20=makeQuery(id+"F0.imprint","IMPRINT",FACE,{"disambiguationData":[TD([[makeQuery(id+"F0.imprint","IMPRINT",EDGE,{"derivedFrom":subQ5}),1.0]])]});}
            var Q21;
            Q21=makeQuery(id+"F0.imprint","IMPRINT",FACE,{"disambiguationData":[TD([[makeQuery(id+"F0.imprint","IMPRINT",EDGE,{"derivedFrom":sQuery(id+"F0.wireOp",EDGE,"E401")}),1.0]])]});
            var Q22;
            {var subQ0=sQuery(id+"F0.wireOp",EDGE,"E422");Q22=makeQuery(id+"F0.imprint","IMPRINT",FACE,{"disambiguationData":[TD([[makeQuery(id+"F0.imprint","IMPRINT",EDGE,{"derivedFrom":subQ0}),-1.0]])]});}
            var Q23;
            Q23=makeQuery(id+"F0.imprint","IMPRINT",FACE,{"disambiguationData":[TD([[makeQuery(id+"F0.imprint","IMPRINT",EDGE,{"derivedFrom":sQuery(id+"F0.wireOp",EDGE,"E366")}),1.0]])]});
            var Q24;
            {var subQ5=sQuery(id+"F0.wireOp",EDGE,"E386");Q24=makeQuery(id+"F0.imprint","IMPRINT",FACE,{"disambiguationData":[TD([[makeQuery(id+"F0.imprint","IMPRINT",EDGE,{"derivedFrom":subQ5}),1.0]])]});}
            var Q25;
            {var subQ10=sQuery(id+"F0.wireOp",EDGE,"E386");Q25=makeQuery(id+"F0.imprint","IMPRINT",FACE,{"disambiguationData":[TD([[makeQuery(id+"F0.imprint","IMPRINT",EDGE,{"derivedFrom":subQ10}),-1.0]])]});}
            var Q26;
            {var subQ5=sQuery(id+"F0.wireOp",EDGE,"E119");Q26=makeQuery(id+"F0.imprint","IMPRINT",FACE,{"disambiguationData":[TD([[makeQuery(id+"F0.imprint","IMPRINT",EDGE,{"derivedFrom":subQ5}),1.0]])]});}
            var Q27;
            {var subQ0=sQuery(id+"F0.wireOp",EDGE,"E353");var subQ1=sQuery(id+"F0.wireOp",EDGE,"E13");var subQ2=makeQuery(id+"F0.imprint","INTERSECT",VERTEX,{"derivedFrom":[subQ1,subQ0]});Q27=makeQuery(id+"F0.imprint","IMPRINT",FACE,{"disambiguationData":[TD([[makeQuery(id+"F0.imprint","IMPRINT",EDGE,{"disambiguationData":[TD([[subQ2,1.0]])],"derivedFrom":subQ1}),1.0]])]});}
            var Q28;
            {var subQ0=sQuery(id+"F0.wireOp",EDGE,"E340");var subQ1=sQuery(id+"F0.wireOp",EDGE,"E13");var subQ2=makeQuery(id+"F0.imprint","INTERSECT",VERTEX,{"derivedFrom":[subQ1,subQ0]});Q28=makeQuery(id+"F0.imprint","IMPRINT",FACE,{"disambiguationData":[TD([[makeQuery(id+"F0.imprint","IMPRINT",EDGE,{"disambiguationData":[TD([[subQ2,-1.0]])],"derivedFrom":subQ1}),-1.0]])]});}
            var Q29;
            {var subQ0=sQuery(id+"F0.wireOp",EDGE,"E353");var subQ1=sQuery(id+"F0.wireOp",EDGE,"E0");var subQ2=makeQuery(id+"F0.imprint","INTERSECT",VERTEX,{"derivedFrom":[subQ1,subQ0]});Q29=makeQuery(id+"F0.imprint","IMPRINT",FACE,{"disambiguationData":[TD([[makeQuery(id+"F0.imprint","IMPRINT",EDGE,{"disambiguationData":[TD([[subQ2,-1.0]])],"derivedFrom":subQ1}),-1.0]])]});}
            var Q30;
            {var subQ0=sQuery(id+"F0.wireOp",EDGE,"E183");var subQ1=sQuery(id+"F0.wireOp",EDGE,"E0");var subQ2=makeQuery(id+"F0.imprint","INTERSECT",VERTEX,{"derivedFrom":[subQ1,subQ0]});Q30=makeQuery(id+"F0.imprint","IMPRINT",FACE,{"disambiguationData":[TD([[makeQuery(id+"F0.imprint","IMPRINT",EDGE,{"disambiguationData":[TD([[subQ2,-1.0]])],"derivedFrom":subQ1}),1.0]])]});}
            var Q31;
            {var subQ0=sQuery(id+"F0.wireOp",EDGE,"E340");var subQ1=sQuery(id+"F0.wireOp",EDGE,"E0");var subQ2=makeQuery(id+"F0.imprint","INTERSECT",VERTEX,{"derivedFrom":[subQ1,subQ0]});Q31=makeQuery(id+"F0.imprint","IMPRINT",FACE,{"disambiguationData":[TD([[makeQuery(id+"F0.imprint","IMPRINT",EDGE,{"disambiguationData":[TD([[subQ2,1.0]])],"derivedFrom":subQ1}),1.0]])]});}
            var Q32;
            {var subQ0=sQuery(id+"F0.wireOp",EDGE,"E170");var subQ1=sQuery(id+"F0.wireOp",EDGE,"E13");var subQ2=makeQuery(id+"F0.imprint","INTERSECT",VERTEX,{"derivedFrom":[subQ1,subQ0]});Q32=makeQuery(id+"F0.imprint","IMPRINT",FACE,{"disambiguationData":[TD([[makeQuery(id+"F0.imprint","IMPRINT",EDGE,{"disambiguationData":[TD([[subQ2,-1.0]])],"derivedFrom":subQ1}),1.0]])]});}
            var Q33;
            {var subQ3=sQuery(id+"F0.wireOp",EDGE,"E353");var subQ6=sQuery(id+"F0.wireOp",EDGE,"E0");var subQ11=makeQuery(id+"F0.imprint","INTERSECT",VERTEX,{"derivedFrom":[subQ6,subQ3]});Q33=makeQuery(id+"F0.imprint","IMPRINT",FACE,{"disambiguationData":[TD([[makeQuery(id+"F0.imprint","IMPRINT",EDGE,{"disambiguationData":[TD([[subQ11,-1.0]])],"derivedFrom":subQ6}),1.0]])]});}
            var Q34;
            {var subQ11=sQuery(id+"F0.wireOp",EDGE,"E217");Q34=makeQuery(id+"F0.imprint","IMPRINT",FACE,{"disambiguationData":[TD([[makeQuery(id+"F0.imprint","IMPRINT",EDGE,{"derivedFrom":subQ11}),-1.0]])]});}
            var Q35;
            {var subQ5=sQuery(id+"F0.wireOp",EDGE,"E217");Q35=makeQuery(id+"F0.imprint","IMPRINT",FACE,{"disambiguationData":[TD([[makeQuery(id+"F0.imprint","IMPRINT",EDGE,{"derivedFrom":subQ5}),1.0]])]});}
            var Q36;
            {var subQ0=sQuery(id+"F0.wireOp",EDGE,"E204");Q36=makeQuery(id+"F0.imprint","IMPRINT",FACE,{"disambiguationData":[TD([[makeQuery(id+"F0.imprint","IMPRINT",EDGE,{"derivedFrom":subQ0}),1.0]])]});}
            var Q37;
            {var subQ0=sQuery(id+"F0.wireOp",EDGE,"E253");Q37=makeQuery(id+"F0.imprint","IMPRINT",FACE,{"disambiguationData":[TD([[makeQuery(id+"F0.imprint","IMPRINT",EDGE,{"derivedFrom":subQ0}),-1.0]])]});}
            var Q38;
            {var subQ5=sQuery(id+"F0.wireOp",EDGE,"E253");Q38=makeQuery(id+"F0.imprint","IMPRINT",FACE,{"disambiguationData":[TD([[makeQuery(id+"F0.imprint","IMPRINT",EDGE,{"derivedFrom":subQ5}),1.0]])]});}
            var Q39;
            Q39=makeQuery(id+"F0.imprint","IMPRINT",FACE,{"disambiguationData":[TD([[makeQuery(id+"F0.imprint","IMPRINT",EDGE,{"derivedFrom":sQuery(id+"F0.wireOp",EDGE,"E196")}),1.0]])]});
            var Q40;
            Q40=makeQuery(id+"F0.imprint","IMPRINT",FACE,{"disambiguationData":[TD([[makeQuery(id+"F0.imprint","IMPRINT",EDGE,{"derivedFrom":sQuery(id+"F0.wireOp",EDGE,"E232")}),1.0]])]});
            var Q41;
            {var subQ5=sQuery(id+"F0.wireOp",EDGE,"E240");Q41=makeQuery(id+"F0.imprint","IMPRINT",FACE,{"disambiguationData":[TD([[makeQuery(id+"F0.imprint","IMPRINT",EDGE,{"derivedFrom":subQ5}),1.0]])]});}
            var Q42;
            {var subQ0=sQuery(id+"F0.wireOp",EDGE,"E171");Q42=makeQuery(id+"F0.imprint","IMPRINT",FACE,{"disambiguationData":[TD([[makeQuery(id+"F0.imprint","IMPRINT",EDGE,{"derivedFrom":subQ0}),1.0]])]});}
            var Q43;
            {var subQ11=sQuery(id+"F0.wireOp",EDGE,"E47");Q43=makeQuery(id+"F0.imprint","IMPRINT",FACE,{"disambiguationData":[TD([[makeQuery(id+"F0.imprint","IMPRINT",EDGE,{"derivedFrom":subQ11}),-1.0]])]});}
            var Q44;
            {var subQ0=sQuery(id+"F0.wireOp",EDGE,"E458");Q44=makeQuery(id+"F0.imprint","IMPRINT",FACE,{"disambiguationData":[TD([[makeQuery(id+"F0.imprint","IMPRINT",EDGE,{"derivedFrom":subQ0}),1.0]])]});}
            var Q45;
            {var subQ0=sQuery(id+"F0.wireOp",EDGE,"E458");Q45=makeQuery(id+"F0.imprint","IMPRINT",FACE,{"disambiguationData":[TD([[makeQuery(id+"F0.imprint","IMPRINT",EDGE,{"derivedFrom":subQ0}),-1.0]])]});}
            var Q46;
            Q46=makeQuery(id+"F0.imprint","IMPRINT",FACE,{"disambiguationData":[TD([[makeQuery(id+"F0.imprint","IMPRINT",EDGE,{"derivedFrom":sQuery(id+"F0.wireOp",EDGE,"E437")}),-1.0]])]});
            var Q47;
            {var subQ5=sQuery(id+"F0.wireOp",EDGE,"E445");Q47=makeQuery(id+"F0.imprint","IMPRINT",FACE,{"disambiguationData":[TD([[makeQuery(id+"F0.imprint","IMPRINT",EDGE,{"derivedFrom":subQ5}),-1.0]])]});}
            var Q48;
            {var subQ5=sQuery(id+"F0.wireOp",EDGE,"E494");Q48=makeQuery(id+"F0.imprint","IMPRINT",FACE,{"disambiguationData":[TD([[makeQuery(id+"F0.imprint","IMPRINT",EDGE,{"derivedFrom":subQ5}),1.0]])]});}
            var Q49;
            {var subQ5=sQuery(id+"F0.wireOp",EDGE,"E494");Q49=makeQuery(id+"F0.imprint","IMPRINT",FACE,{"disambiguationData":[TD([[makeQuery(id+"F0.imprint","IMPRINT",EDGE,{"derivedFrom":subQ5}),-1.0]])]});}
            var Q50;
            Q50=makeQuery(id+"F0.imprint","IMPRINT",FACE,{"disambiguationData":[TD([[makeQuery(id+"F0.imprint","IMPRINT",EDGE,{"derivedFrom":sQuery(id+"F0.wireOp",EDGE,"E473")}),-1.0]])]});
            var Q51;
            {var subQ5=sQuery(id+"F0.wireOp",EDGE,"E481");Q51=makeQuery(id+"F0.imprint","IMPRINT",FACE,{"disambiguationData":[TD([[makeQuery(id+"F0.imprint","IMPRINT",EDGE,{"derivedFrom":subQ5}),-1.0]])]});}
            var Q52;
            {var subQ8=sQuery(id+"F0.wireOp",EDGE,"E354");Q52=makeQuery(id+"F0.imprint","IMPRINT",FACE,{"disambiguationData":[TD([[makeQuery(id+"F0.imprint","IMPRINT",EDGE,{"derivedFrom":subQ8}),1.0]])]});}
            var Q53;
            Q53=makeQuery(id+"F0.imprint","IMPRINT",FACE,{"disambiguationData":[TD([[makeQuery(id+"F0.imprint","IMPRINT",EDGE,{"derivedFrom":sQuery(id+"F0.wireOp",EDGE,"E26")}),1.0]])]});
            var Q54;
            {var subQ5=sQuery(id+"F0.wireOp",EDGE,"E47");Q54=makeQuery(id+"F0.imprint","IMPRINT",FACE,{"disambiguationData":[TD([[makeQuery(id+"F0.imprint","IMPRINT",EDGE,{"derivedFrom":subQ5}),1.0]])]});}
            var Q55;
            {var subQ0=sQuery(id+"F0.wireOp",EDGE,"E34");Q55=makeQuery(id+"F0.imprint","IMPRINT",FACE,{"disambiguationData":[TD([[makeQuery(id+"F0.imprint","IMPRINT",EDGE,{"derivedFrom":subQ0}),1.0]])]});}
            var Q56;
            {var subQ0=sQuery(id+"F0.wireOp",EDGE,"E83");Q56=makeQuery(id+"F0.imprint","IMPRINT",FACE,{"disambiguationData":[TD([[makeQuery(id+"F0.imprint","IMPRINT",EDGE,{"derivedFrom":subQ0}),-1.0]])]});}
            var Q57;
            {var subQ5=sQuery(id+"F0.wireOp",EDGE,"E83");Q57=makeQuery(id+"F0.imprint","IMPRINT",FACE,{"disambiguationData":[TD([[makeQuery(id+"F0.imprint","IMPRINT",EDGE,{"derivedFrom":subQ5}),1.0]])]});}
            var Q58;
            {var subQ5=sQuery(id+"F0.wireOp",EDGE,"E70");Q58=makeQuery(id+"F0.imprint","IMPRINT",FACE,{"disambiguationData":[TD([[makeQuery(id+"F0.imprint","IMPRINT",EDGE,{"derivedFrom":subQ5}),1.0]])]});}
            var Q59;
            {var subQ0=sQuery(id+"F0.wireOp",EDGE,"E1");Q59=makeQuery(id+"F0.imprint","IMPRINT",FACE,{"disambiguationData":[TD([[makeQuery(id+"F0.imprint","IMPRINT",EDGE,{"derivedFrom":subQ0}),1.0]])]});}
            var Q60;
            Q60=makeQuery(id+"F0.imprint","IMPRINT",FACE,{"disambiguationData":[TD([[makeQuery(id+"F0.imprint","IMPRINT",EDGE,{"derivedFrom":sQuery(id+"F0.wireOp",EDGE,"E62")}),1.0]])]});
            extrude(context, id + "F1", {"entities" : qUnion([Q0, Q1, Q2, Q3, Q4, Q5, Q6, Q7, Q8, Q9, Q10, Q11, Q12, Q13, Q14, Q15, Q16, Q17, Q18, Q19, Q20, Q21, Q22, Q23, Q24, Q25, Q26, Q27, Q28, Q29, Q30, Q31, Q32, Q33, Q34, Q35, Q36, Q37, Q38, Q39, Q40, Q41, Q42, Q43, Q44, Q45, Q46, Q47, Q48, Q49, Q50, Q51, Q52, Q53, Q54, Q55, Q56, Q57, Q58, Q59, Q60]), "depth" : 2 * mm});
        }
    });
